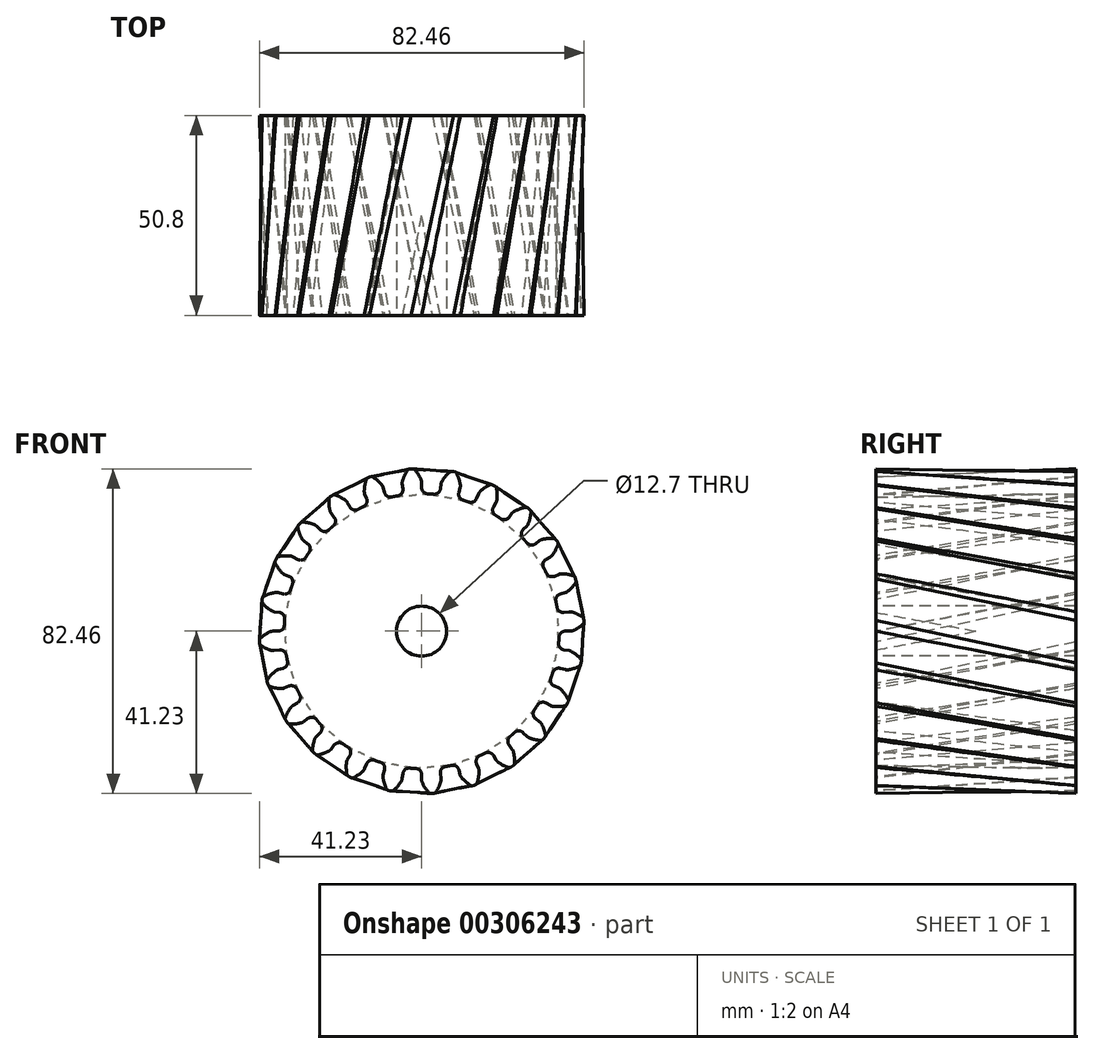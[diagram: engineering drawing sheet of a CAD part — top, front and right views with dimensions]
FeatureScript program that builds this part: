
annotation { "Feature Type Name" : "Feature", "Feature Type Description" : "" }
export const myFeature = defineFeature(function(context is Context, id is Id, definition is map)
    precondition{}
    {
        {
            var Q0;
            Q0=qCreatedBy(makeId("Front.planeOp"),FACE);
            cPlane(context, id + "F0", {"entities" : qUnion([Q0]), "cplaneType" : CPlaneType.OFFSET, "offset" : 50.8 * mm, "width" : 152.4 * mm, "height" : 152.4 * mm});
        }
        {
            var Q0;
            Q0=qCreatedBy(makeId("Front.planeOp"),FACE);
            var sketch = newSketch(context, id + "F1", { "sketchPlane" : qUnion([Q0])});
            skArc(sketch, "E0", {"start": v(-6.06, 34.4) * mm, "mid": v(-6.81, 34.25) * mm, "end": v(-7.56, 34.1) * mm});
            skArc(sketch, "E1.trimOffspring", {"start": v(-0.13, 38.41) * mm, "mid": v(-0.86, 39.8) * mm, "end": v(-1.82, 41.06) * mm});
            skLineSegment(sketch, "E2", {"start": v(0, 37.8) * mm, "end": v(0, 36.48) * mm});
            skLineSegment(sketch, "E3", {"start": v(-2.2, 41.23) * mm, "end": v(-2.7, 41.23) * mm});
            skLineSegment(sketch, "E4.MirrorCS", {"start": v(-3.2, 41.16) * mm, "end": v(-2.7, 41.23) * mm});
            skArc(sketch, "E5.MirrorCS", {"start": v(-4.89, 38.1) * mm, "mid": v(-4.34, 39.58) * mm, "end": v(-3.56, 40.95) * mm});
            skLineSegment(sketch, "E6.MirrorCS", {"start": v(-4.93, 37.47) * mm, "end": v(-4.76, 36.17) * mm});
            skPoint(sketch, "E7.visualSharp", {"position": v(0, 34.93) * mm});
            skArc(sketch, "E7.filletArc", {"start": v(0, 35.2) * mm, "mid": v(0.08, 35) * mm, "end": v(0.28, 34.92) * mm});
            skArc(sketch, "E8.filletArc", {"start": v(0, 36.48) * mm, "mid": v(0.44, 35.38) * mm, "end": v(1.52, 34.9) * mm});
            skPoint(sketch, "E9.visualSharp", {"position": v(-4.56, 34.63) * mm});
            skArc(sketch, "E9.filletArc", {"start": v(-6.06, 34.4) * mm, "mid": v(-5.06, 35.02) * mm, "end": v(-4.76, 36.17) * mm});
            skPoint(sketch, "E10.visualSharp", {"position": v(-4.97, 37.77) * mm});
            skArc(sketch, "E10.filletArc", {"start": v(-4.89, 38.1) * mm, "mid": v(-4.94, 37.79) * mm, "end": v(-4.93, 37.47) * mm});
            skPoint(sketch, "E11.visualSharp", {"position": v(0, 38.1) * mm});
            skArc(sketch, "E11.filletArc", {"start": v(0, 37.8) * mm, "mid": v(-0.03, 38.1) * mm, "end": v(-0.13, 38.41) * mm});
            skPoint(sketch, "E12.visualSharp", {"position": v(-3.43, 41.13) * mm});
            skArc(sketch, "E12.filletArc", {"start": v(-3.2, 41.16) * mm, "mid": v(-3.4, 41.1) * mm, "end": v(-3.56, 40.95) * mm});
            skPoint(sketch, "E13.visualSharp", {"position": v(-1.97, 41.23) * mm});
            skArc(sketch, "E13.filletArc", {"start": v(-1.82, 41.06) * mm, "mid": v(-1.99, 41.18) * mm, "end": v(-2.2, 41.23) * mm});
            skArc(sketch, "E14.1.0", {"start": v(-9.44, 35.24) * mm, "mid": v(-8.73, 34.29) * mm, "end": v(-7.56, 34.1) * mm});
            skLineSegment(sketch, "E14.1.1", {"start": v(-9.78, 36.5) * mm, "end": v(-9.44, 35.24) * mm});
            skLineSegment(sketch, "E14.1.2", {"start": v(-14.46, 34.91) * mm, "end": v(-13.96, 33.7) * mm});
            skLineSegment(sketch, "E14.1.3", {"start": v(-12.79, 39.26) * mm, "end": v(-13.28, 39.12) * mm});
            skPoint(sketch, "E14.1.4", {"position": v(-12.58, 39.31) * mm});
            skPoint(sketch, "E14.1.5", {"position": v(-13.96, 38.84) * mm});
            skLineSegment(sketch, "E14.1.6", {"start": v(-13.75, 38.93) * mm, "end": v(-13.28, 39.12) * mm});
            skArc(sketch, "E14.1.7", {"start": v(-10.06, 37.07) * mm, "mid": v(-11.14, 38.23) * mm, "end": v(-12.38, 39.2) * mm});
            skPoint(sketch, "E14.1.8", {"position": v(-9.86, 36.8) * mm});
            skArc(sketch, "E14.1.9", {"start": v(-14.58, 35.54) * mm, "mid": v(-14.44, 37.1) * mm, "end": v(-14.03, 38.63) * mm});
            skPoint(sketch, "E14.1.10", {"position": v(-14.58, 35.2) * mm});
            skArc(sketch, "E14.1.11", {"start": v(-14.58, 35.54) * mm, "mid": v(-14.55, 35.22) * mm, "end": v(-14.46, 34.91) * mm});
            skArc(sketch, "E14.1.12", {"start": v(-9.78, 36.5) * mm, "mid": v(-9.9, 36.8) * mm, "end": v(-10.06, 37.07) * mm});
            skArc(sketch, "E14.1.13", {"start": v(-12.38, 39.2) * mm, "mid": v(-12.58, 39.27) * mm, "end": v(-12.79, 39.26) * mm});
            skArc(sketch, "E14.1.14", {"start": v(-13.75, 38.93) * mm, "mid": v(-13.92, 38.8) * mm, "end": v(-14.03, 38.63) * mm});
            skArc(sketch, "E14.1.15", {"start": v(-14.76, 31.65) * mm, "mid": v(-13.95, 32.52) * mm, "end": v(-13.96, 33.7) * mm});
            skArc(sketch, "E14.2.0", {"start": v(-18.24, 31.6) * mm, "mid": v(-17.3, 30.86) * mm, "end": v(-16.13, 30.98) * mm});
            skLineSegment(sketch, "E14.2.1", {"start": v(-18.9, 32.73) * mm, "end": v(-18.24, 31.6) * mm});
            skLineSegment(sketch, "E14.2.2", {"start": v(-23, 29.98) * mm, "end": v(-22.2, 28.94) * mm});
            skLineSegment(sketch, "E14.2.3", {"start": v(-22.51, 34.6) * mm, "end": v(-22.95, 34.35) * mm});
            skPoint(sketch, "E14.2.4", {"position": v(-22.32, 34.72) * mm});
            skPoint(sketch, "E14.2.5", {"position": v(-23.53, 33.9) * mm});
            skLineSegment(sketch, "E14.2.6", {"start": v(-23.36, 34.04) * mm, "end": v(-22.95, 34.35) * mm});
            skArc(sketch, "E14.2.7", {"start": v(-19.32, 33.2) * mm, "mid": v(-20.65, 34.04) * mm, "end": v(-22.1, 34.65) * mm});
            skPoint(sketch, "E14.2.8", {"position": v(-19.05, 33) * mm});
            skArc(sketch, "E14.2.9", {"start": v(-23.28, 30.55) * mm, "mid": v(-23.55, 32.1) * mm, "end": v(-23.55, 33.68) * mm});
            skPoint(sketch, "E14.2.10", {"position": v(-23.2, 30.23) * mm});
            skArc(sketch, "E14.2.11", {"start": v(-23.28, 30.55) * mm, "mid": v(-23.17, 30.25) * mm, "end": v(-23, 29.98) * mm});
            skArc(sketch, "E14.2.12", {"start": v(-18.9, 32.73) * mm, "mid": v(-19.08, 32.99) * mm, "end": v(-19.32, 33.2) * mm});
            skArc(sketch, "E14.2.13", {"start": v(-22.1, 34.65) * mm, "mid": v(-22.31, 34.67) * mm, "end": v(-22.51, 34.6) * mm});
            skArc(sketch, "E14.2.14", {"start": v(-23.36, 34.04) * mm, "mid": v(-23.5, 33.88) * mm, "end": v(-23.55, 33.68) * mm});
            skArc(sketch, "E14.2.15", {"start": v(-22.45, 26.76) * mm, "mid": v(-21.89, 27.8) * mm, "end": v(-22.2, 28.94) * mm});
            skArc(sketch, "E15.3.3.0", {"start": v(-25.8, 25.8) * mm, "mid": v(-24.7, 25.33) * mm, "end": v(-23.6, 25.75) * mm});
            skLineSegment(sketch, "E15.4.3.0", {"start": v(-26.72, 26.72) * mm, "end": v(-25.8, 25.8) * mm});
            skLineSegment(sketch, "E15.7.3.0", {"start": v(-29.98, 23) * mm, "end": v(-28.94, 22.2) * mm});
            skLineSegment(sketch, "E15.10.3.0", {"start": v(-30.7, 27.6) * mm, "end": v(-31.06, 27.24) * mm});
            skPoint(sketch, "E15.13.3.0", {"position": v(-30.55, 27.76) * mm});
            skPoint(sketch, "E15.14.3.0", {"position": v(-31.5, 26.66) * mm});
            skLineSegment(sketch, "E15.15.3.0", {"start": v(-31.37, 26.84) * mm, "end": v(-31.06, 27.24) * mm});
            skArc(sketch, "E15.18.3.0", {"start": v(-27.25, 27.07) * mm, "mid": v(-28.76, 27.54) * mm, "end": v(-30.32, 27.75) * mm});
            skPoint(sketch, "E15.22.3.0", {"position": v(-26.94, 26.94) * mm});
            skArc(sketch, "E15.23.3.0", {"start": v(-30.4, 23.49) * mm, "mid": v(-31.06, 24.92) * mm, "end": v(-31.47, 26.44) * mm});
            skPoint(sketch, "E15.27.3.0", {"position": v(-30.23, 23.2) * mm});
            skArc(sketch, "E15.28.3.0", {"start": v(-30.4, 23.49) * mm, "mid": v(-30.21, 23.22) * mm, "end": v(-29.98, 23) * mm});
            skArc(sketch, "E15.32.3.0", {"start": v(-26.72, 26.72) * mm, "mid": v(-26.97, 26.92) * mm, "end": v(-27.25, 27.07) * mm});
            skArc(sketch, "E15.36.3.0", {"start": v(-30.32, 27.75) * mm, "mid": v(-30.53, 27.72) * mm, "end": v(-30.7, 27.6) * mm});
            skArc(sketch, "E15.40.3.0", {"start": v(-31.37, 26.84) * mm, "mid": v(-31.46, 26.65) * mm, "end": v(-31.47, 26.44) * mm});
            skArc(sketch, "E15.44.3.0", {"start": v(-28.6, 20.04) * mm, "mid": v(-28.34, 21.19) * mm, "end": v(-28.94, 22.2) * mm});
            skArc(sketch, "E15.3.4.0", {"start": v(-31.6, 18.24) * mm, "mid": v(-30.42, 18.07) * mm, "end": v(-29.46, 18.76) * mm});
            skLineSegment(sketch, "E15.4.4.0", {"start": v(-32.73, 18.9) * mm, "end": v(-31.6, 18.24) * mm});
            skLineSegment(sketch, "E15.7.4.0", {"start": v(-34.91, 14.46) * mm, "end": v(-33.7, 13.96) * mm});
            skLineSegment(sketch, "E15.10.4.0", {"start": v(-36.8, 18.71) * mm, "end": v(-37.06, 18.27) * mm});
            skPoint(sketch, "E15.13.4.0", {"position": v(-36.7, 18.9) * mm});
            skPoint(sketch, "E15.14.4.0", {"position": v(-37.33, 17.6) * mm});
            skLineSegment(sketch, "E15.15.4.0", {"start": v(-37.25, 17.8) * mm, "end": v(-37.06, 18.27) * mm});
            skArc(sketch, "E15.18.4.0", {"start": v(-33.33, 19.1) * mm, "mid": v(-34.9, 19.16) * mm, "end": v(-36.47, 18.96) * mm});
            skPoint(sketch, "E15.22.4.0", {"position": v(-33, 19.05) * mm});
            skArc(sketch, "E15.23.4.0", {"start": v(-35.44, 14.82) * mm, "mid": v(-36.45, 16.03) * mm, "end": v(-37.24, 17.4) * mm});
            skPoint(sketch, "E15.27.4.0", {"position": v(-35.2, 14.58) * mm});
            skArc(sketch, "E15.28.4.0", {"start": v(-35.44, 14.82) * mm, "mid": v(-35.2, 14.61) * mm, "end": v(-34.91, 14.46) * mm});
            skArc(sketch, "E15.32.4.0", {"start": v(-32.73, 18.9) * mm, "mid": v(-33.02, 19.03) * mm, "end": v(-33.33, 19.1) * mm});
            skArc(sketch, "E15.36.4.0", {"start": v(-36.47, 18.96) * mm, "mid": v(-36.66, 18.87) * mm, "end": v(-36.8, 18.71) * mm});
            skArc(sketch, "E15.40.4.0", {"start": v(-37.25, 17.8) * mm, "mid": v(-37.29, 17.6) * mm, "end": v(-37.24, 17.4) * mm});
            skArc(sketch, "E15.44.4.0", {"start": v(-32.82, 11.95) * mm, "mid": v(-32.86, 13.13) * mm, "end": v(-33.7, 13.96) * mm});
            skArc(sketch, "E15.3.5.0", {"start": v(-35.24, 9.44) * mm, "mid": v(-34.06, 9.58) * mm, "end": v(-33.31, 10.5) * mm});
            skLineSegment(sketch, "E15.4.5.0", {"start": v(-36.5, 9.78) * mm, "end": v(-35.24, 9.44) * mm});
            skLineSegment(sketch, "E15.7.5.0", {"start": v(-37.47, 4.93) * mm, "end": v(-36.17, 4.76) * mm});
            skLineSegment(sketch, "E15.10.5.0", {"start": v(-40.4, 8.55) * mm, "end": v(-40.52, 8.06) * mm});
            skPoint(sketch, "E15.13.5.0", {"position": v(-40.33, 8.77) * mm});
            skPoint(sketch, "E15.14.5.0", {"position": v(-40.62, 7.34) * mm});
            skLineSegment(sketch, "E15.15.5.0", {"start": v(-40.59, 7.56) * mm, "end": v(-40.52, 8.06) * mm});
            skArc(sketch, "E15.18.5.0", {"start": v(-37.14, 9.82) * mm, "mid": v(-38.67, 9.47) * mm, "end": v(-40.13, 8.87) * mm});
            skPoint(sketch, "E15.22.5.0", {"position": v(-36.8, 9.86) * mm});
            skArc(sketch, "E15.23.5.0", {"start": v(-38.07, 5.14) * mm, "mid": v(-39.35, 6.05) * mm, "end": v(-40.47, 7.16) * mm});
            skPoint(sketch, "E15.27.5.0", {"position": v(-37.77, 4.97) * mm});
            skArc(sketch, "E15.28.5.0", {"start": v(-38.07, 5.14) * mm, "mid": v(-37.78, 5) * mm, "end": v(-37.47, 4.93) * mm});
            skArc(sketch, "E15.32.5.0", {"start": v(-36.5, 9.78) * mm, "mid": v(-36.82, 9.83) * mm, "end": v(-37.14, 9.82) * mm});
            skArc(sketch, "E15.36.5.0", {"start": v(-40.13, 8.87) * mm, "mid": v(-40.3, 8.74) * mm, "end": v(-40.4, 8.55) * mm});
            skArc(sketch, "E15.40.5.0", {"start": v(-40.59, 7.56) * mm, "mid": v(-40.57, 7.35) * mm, "end": v(-40.47, 7.16) * mm});
            skArc(sketch, "E15.44.5.0", {"start": v(-34.8, 3.05) * mm, "mid": v(-35.13, 4.18) * mm, "end": v(-36.17, 4.76) * mm});
            skArc(sketch, "E15.3.6.0", {"start": v(-36.48, 0) * mm, "mid": v(-35.38, 0.44) * mm, "end": v(-34.9, 1.52) * mm});
            skLineSegment(sketch, "E15.4.6.0", {"start": v(-37.8, 0) * mm, "end": v(-36.48, 0) * mm});
            skLineSegment(sketch, "E15.7.6.0", {"start": v(-37.47, -4.93) * mm, "end": v(-36.17, -4.76) * mm});
            skLineSegment(sketch, "E15.10.6.0", {"start": v(-41.23, -2.2) * mm, "end": v(-41.23, -2.7) * mm});
            skPoint(sketch, "E15.13.6.0", {"position": v(-41.23, -1.97) * mm});
            skPoint(sketch, "E15.14.6.0", {"position": v(-41.13, -3.43) * mm});
            skLineSegment(sketch, "E15.15.6.0", {"start": v(-41.16, -3.2) * mm, "end": v(-41.23, -2.7) * mm});
            skArc(sketch, "E15.18.6.0", {"start": v(-38.41, -0.13) * mm, "mid": v(-39.8, -0.86) * mm, "end": v(-41.06, -1.82) * mm});
            skPoint(sketch, "E15.22.6.0", {"position": v(-38.1, 0) * mm});
            skArc(sketch, "E15.23.6.0", {"start": v(-38.1, -4.89) * mm, "mid": v(-39.58, -4.34) * mm, "end": v(-40.95, -3.56) * mm});
            skPoint(sketch, "E15.27.6.0", {"position": v(-37.77, -4.97) * mm});
            skArc(sketch, "E15.28.6.0", {"start": v(-38.1, -4.89) * mm, "mid": v(-37.79, -4.94) * mm, "end": v(-37.47, -4.93) * mm});
            skArc(sketch, "E15.32.6.0", {"start": v(-37.8, 0) * mm, "mid": v(-38.1, -0.03) * mm, "end": v(-38.41, -0.13) * mm});
            skArc(sketch, "E15.36.6.0", {"start": v(-41.06, -1.82) * mm, "mid": v(-41.18, -1.99) * mm, "end": v(-41.23, -2.2) * mm});
            skArc(sketch, "E15.40.6.0", {"start": v(-41.16, -3.2) * mm, "mid": v(-41.1, -3.4) * mm, "end": v(-40.95, -3.56) * mm});
            skArc(sketch, "E15.44.6.0", {"start": v(-34.4, -6.06) * mm, "mid": v(-35.02, -5.06) * mm, "end": v(-36.17, -4.76) * mm});
            skArc(sketch, "E15.3.7.0", {"start": v(-35.24, -9.44) * mm, "mid": v(-34.29, -8.73) * mm, "end": v(-34.1, -7.56) * mm});
            skLineSegment(sketch, "E15.4.7.0", {"start": v(-36.5, -9.78) * mm, "end": v(-35.24, -9.44) * mm});
            skLineSegment(sketch, "E15.7.7.0", {"start": v(-34.91, -14.46) * mm, "end": v(-33.7, -13.96) * mm});
            skLineSegment(sketch, "E15.10.7.0", {"start": v(-39.26, -12.79) * mm, "end": v(-39.12, -13.28) * mm});
            skPoint(sketch, "E15.13.7.0", {"position": v(-39.31, -12.58) * mm});
            skPoint(sketch, "E15.14.7.0", {"position": v(-38.84, -13.96) * mm});
            skLineSegment(sketch, "E15.15.7.0", {"start": v(-38.93, -13.75) * mm, "end": v(-39.12, -13.28) * mm});
            skArc(sketch, "E15.18.7.0", {"start": v(-37.07, -10.06) * mm, "mid": v(-38.23, -11.14) * mm, "end": v(-39.2, -12.38) * mm});
            skPoint(sketch, "E15.22.7.0", {"position": v(-36.8, -9.86) * mm});
            skArc(sketch, "E15.23.7.0", {"start": v(-35.54, -14.58) * mm, "mid": v(-37.1, -14.44) * mm, "end": v(-38.63, -14.03) * mm});
            skPoint(sketch, "E15.27.7.0", {"position": v(-35.2, -14.58) * mm});
            skArc(sketch, "E15.28.7.0", {"start": v(-35.54, -14.58) * mm, "mid": v(-35.22, -14.55) * mm, "end": v(-34.91, -14.46) * mm});
            skArc(sketch, "E15.32.7.0", {"start": v(-36.5, -9.78) * mm, "mid": v(-36.8, -9.9) * mm, "end": v(-37.07, -10.06) * mm});
            skArc(sketch, "E15.36.7.0", {"start": v(-39.2, -12.38) * mm, "mid": v(-39.27, -12.58) * mm, "end": v(-39.26, -12.79) * mm});
            skArc(sketch, "E15.40.7.0", {"start": v(-38.93, -13.75) * mm, "mid": v(-38.8, -13.92) * mm, "end": v(-38.63, -14.03) * mm});
            skArc(sketch, "E15.44.7.0", {"start": v(-31.65, -14.76) * mm, "mid": v(-32.52, -13.95) * mm, "end": v(-33.7, -13.96) * mm});
            skArc(sketch, "E15.3.8.0", {"start": v(-31.6, -18.24) * mm, "mid": v(-30.86, -17.3) * mm, "end": v(-30.98, -16.13) * mm});
            skLineSegment(sketch, "E15.4.8.0", {"start": v(-32.73, -18.9) * mm, "end": v(-31.6, -18.24) * mm});
            skLineSegment(sketch, "E15.7.8.0", {"start": v(-29.98, -23) * mm, "end": v(-28.94, -22.2) * mm});
            skLineSegment(sketch, "E15.10.8.0", {"start": v(-34.6, -22.51) * mm, "end": v(-34.35, -22.95) * mm});
            skPoint(sketch, "E15.13.8.0", {"position": v(-34.72, -22.32) * mm});
            skPoint(sketch, "E15.14.8.0", {"position": v(-33.9, -23.53) * mm});
            skLineSegment(sketch, "E15.15.8.0", {"start": v(-34.04, -23.36) * mm, "end": v(-34.35, -22.95) * mm});
            skArc(sketch, "E15.18.8.0", {"start": v(-33.2, -19.32) * mm, "mid": v(-34.04, -20.65) * mm, "end": v(-34.65, -22.1) * mm});
            skPoint(sketch, "E15.22.8.0", {"position": v(-33, -19.05) * mm});
            skArc(sketch, "E15.23.8.0", {"start": v(-30.55, -23.28) * mm, "mid": v(-32.1, -23.55) * mm, "end": v(-33.68, -23.55) * mm});
            skPoint(sketch, "E15.27.8.0", {"position": v(-30.23, -23.2) * mm});
            skArc(sketch, "E15.28.8.0", {"start": v(-30.55, -23.28) * mm, "mid": v(-30.25, -23.17) * mm, "end": v(-29.98, -23) * mm});
            skArc(sketch, "E15.32.8.0", {"start": v(-32.73, -18.9) * mm, "mid": v(-32.99, -19.08) * mm, "end": v(-33.2, -19.32) * mm});
            skArc(sketch, "E15.36.8.0", {"start": v(-34.65, -22.1) * mm, "mid": v(-34.67, -22.31) * mm, "end": v(-34.6, -22.51) * mm});
            skArc(sketch, "E15.40.8.0", {"start": v(-34.04, -23.36) * mm, "mid": v(-33.88, -23.5) * mm, "end": v(-33.68, -23.55) * mm});
            skArc(sketch, "E15.44.8.0", {"start": v(-26.76, -22.45) * mm, "mid": v(-27.8, -21.89) * mm, "end": v(-28.94, -22.2) * mm});
            skArc(sketch, "E15.3.9.0", {"start": v(-25.8, -25.8) * mm, "mid": v(-25.33, -24.7) * mm, "end": v(-25.75, -23.6) * mm});
            skLineSegment(sketch, "E15.4.9.0", {"start": v(-26.72, -26.72) * mm, "end": v(-25.8, -25.8) * mm});
            skLineSegment(sketch, "E15.7.9.0", {"start": v(-23, -29.98) * mm, "end": v(-22.2, -28.94) * mm});
            skLineSegment(sketch, "E15.10.9.0", {"start": v(-27.6, -30.7) * mm, "end": v(-27.24, -31.06) * mm});
            skPoint(sketch, "E15.13.9.0", {"position": v(-27.76, -30.55) * mm});
            skPoint(sketch, "E15.14.9.0", {"position": v(-26.66, -31.5) * mm});
            skLineSegment(sketch, "E15.15.9.0", {"start": v(-26.84, -31.37) * mm, "end": v(-27.24, -31.06) * mm});
            skArc(sketch, "E15.18.9.0", {"start": v(-27.07, -27.25) * mm, "mid": v(-27.54, -28.76) * mm, "end": v(-27.75, -30.32) * mm});
            skPoint(sketch, "E15.22.9.0", {"position": v(-26.94, -26.94) * mm});
            skArc(sketch, "E15.23.9.0", {"start": v(-23.49, -30.4) * mm, "mid": v(-24.92, -31.06) * mm, "end": v(-26.44, -31.47) * mm});
            skPoint(sketch, "E15.27.9.0", {"position": v(-23.2, -30.23) * mm});
            skArc(sketch, "E15.28.9.0", {"start": v(-23.49, -30.4) * mm, "mid": v(-23.22, -30.21) * mm, "end": v(-23, -29.98) * mm});
            skArc(sketch, "E15.32.9.0", {"start": v(-26.72, -26.72) * mm, "mid": v(-26.92, -26.97) * mm, "end": v(-27.07, -27.25) * mm});
            skArc(sketch, "E15.36.9.0", {"start": v(-27.75, -30.32) * mm, "mid": v(-27.72, -30.53) * mm, "end": v(-27.6, -30.7) * mm});
            skArc(sketch, "E15.40.9.0", {"start": v(-26.84, -31.37) * mm, "mid": v(-26.65, -31.46) * mm, "end": v(-26.44, -31.47) * mm});
            skArc(sketch, "E15.44.9.0", {"start": v(-20.04, -28.6) * mm, "mid": v(-21.19, -28.34) * mm, "end": v(-22.2, -28.94) * mm});
            skArc(sketch, "E15.3.10.0", {"start": v(-18.24, -31.6) * mm, "mid": v(-18.07, -30.42) * mm, "end": v(-18.76, -29.46) * mm});
            skLineSegment(sketch, "E15.4.10.0", {"start": v(-18.9, -32.73) * mm, "end": v(-18.24, -31.6) * mm});
            skLineSegment(sketch, "E15.7.10.0", {"start": v(-14.46, -34.91) * mm, "end": v(-13.96, -33.7) * mm});
            skLineSegment(sketch, "E15.10.10.0", {"start": v(-18.71, -36.8) * mm, "end": v(-18.27, -37.06) * mm});
            skPoint(sketch, "E15.13.10.0", {"position": v(-18.9, -36.7) * mm});
            skPoint(sketch, "E15.14.10.0", {"position": v(-17.6, -37.33) * mm});
            skLineSegment(sketch, "E15.15.10.0", {"start": v(-17.8, -37.25) * mm, "end": v(-18.27, -37.06) * mm});
            skArc(sketch, "E15.18.10.0", {"start": v(-19.1, -33.33) * mm, "mid": v(-19.16, -34.9) * mm, "end": v(-18.96, -36.47) * mm});
            skPoint(sketch, "E15.22.10.0", {"position": v(-19.05, -33) * mm});
            skArc(sketch, "E15.23.10.0", {"start": v(-14.82, -35.44) * mm, "mid": v(-16.03, -36.45) * mm, "end": v(-17.4, -37.24) * mm});
            skPoint(sketch, "E15.27.10.0", {"position": v(-14.58, -35.2) * mm});
            skArc(sketch, "E15.28.10.0", {"start": v(-14.82, -35.44) * mm, "mid": v(-14.61, -35.2) * mm, "end": v(-14.46, -34.91) * mm});
            skArc(sketch, "E15.32.10.0", {"start": v(-18.9, -32.73) * mm, "mid": v(-19.03, -33.02) * mm, "end": v(-19.1, -33.33) * mm});
            skArc(sketch, "E15.36.10.0", {"start": v(-18.96, -36.47) * mm, "mid": v(-18.87, -36.66) * mm, "end": v(-18.71, -36.8) * mm});
            skArc(sketch, "E15.40.10.0", {"start": v(-17.8, -37.25) * mm, "mid": v(-17.6, -37.29) * mm, "end": v(-17.4, -37.24) * mm});
            skArc(sketch, "E15.44.10.0", {"start": v(-11.95, -32.82) * mm, "mid": v(-13.13, -32.86) * mm, "end": v(-13.96, -33.7) * mm});
            skArc(sketch, "E15.3.11.0", {"start": v(-9.44, -35.24) * mm, "mid": v(-9.58, -34.06) * mm, "end": v(-10.5, -33.31) * mm});
            skLineSegment(sketch, "E15.4.11.0", {"start": v(-9.78, -36.5) * mm, "end": v(-9.44, -35.24) * mm});
            skLineSegment(sketch, "E15.7.11.0", {"start": v(-4.93, -37.47) * mm, "end": v(-4.76, -36.17) * mm});
            skLineSegment(sketch, "E15.10.11.0", {"start": v(-8.55, -40.4) * mm, "end": v(-8.06, -40.52) * mm});
            skPoint(sketch, "E15.13.11.0", {"position": v(-8.77, -40.33) * mm});
            skPoint(sketch, "E15.14.11.0", {"position": v(-7.34, -40.62) * mm});
            skLineSegment(sketch, "E15.15.11.0", {"start": v(-7.56, -40.59) * mm, "end": v(-8.06, -40.52) * mm});
            skArc(sketch, "E15.18.11.0", {"start": v(-9.82, -37.14) * mm, "mid": v(-9.47, -38.67) * mm, "end": v(-8.87, -40.13) * mm});
            skPoint(sketch, "E15.22.11.0", {"position": v(-9.86, -36.8) * mm});
            skArc(sketch, "E15.23.11.0", {"start": v(-5.14, -38.07) * mm, "mid": v(-6.05, -39.35) * mm, "end": v(-7.16, -40.47) * mm});
            skPoint(sketch, "E15.27.11.0", {"position": v(-4.97, -37.77) * mm});
            skArc(sketch, "E15.28.11.0", {"start": v(-5.14, -38.07) * mm, "mid": v(-5, -37.78) * mm, "end": v(-4.93, -37.47) * mm});
            skArc(sketch, "E15.32.11.0", {"start": v(-9.78, -36.5) * mm, "mid": v(-9.83, -36.82) * mm, "end": v(-9.82, -37.14) * mm});
            skArc(sketch, "E15.36.11.0", {"start": v(-8.87, -40.13) * mm, "mid": v(-8.74, -40.3) * mm, "end": v(-8.55, -40.4) * mm});
            skArc(sketch, "E15.40.11.0", {"start": v(-7.56, -40.59) * mm, "mid": v(-7.35, -40.57) * mm, "end": v(-7.16, -40.47) * mm});
            skArc(sketch, "E15.44.11.0", {"start": v(-3.05, -34.8) * mm, "mid": v(-4.18, -35.13) * mm, "end": v(-4.76, -36.17) * mm});
            skArc(sketch, "E15.3.12.0", {"start": v(0, -36.48) * mm, "mid": v(-0.44, -35.38) * mm, "end": v(-1.52, -34.9) * mm});
            skLineSegment(sketch, "E15.4.12.0", {"start": v(0, -37.8) * mm, "end": v(0, -36.48) * mm});
            skLineSegment(sketch, "E15.7.12.0", {"start": v(4.93, -37.47) * mm, "end": v(4.76, -36.17) * mm});
            skLineSegment(sketch, "E15.10.12.0", {"start": v(2.2, -41.23) * mm, "end": v(2.7, -41.23) * mm});
            skPoint(sketch, "E15.13.12.0", {"position": v(1.97, -41.23) * mm});
            skPoint(sketch, "E15.14.12.0", {"position": v(3.43, -41.13) * mm});
            skLineSegment(sketch, "E15.15.12.0", {"start": v(3.2, -41.16) * mm, "end": v(2.7, -41.23) * mm});
            skArc(sketch, "E15.18.12.0", {"start": v(0.13, -38.41) * mm, "mid": v(0.86, -39.8) * mm, "end": v(1.82, -41.06) * mm});
            skPoint(sketch, "E15.22.12.0", {"position": v(0, -38.1) * mm});
            skArc(sketch, "E15.23.12.0", {"start": v(4.89, -38.1) * mm, "mid": v(4.34, -39.58) * mm, "end": v(3.56, -40.95) * mm});
            skPoint(sketch, "E15.27.12.0", {"position": v(4.97, -37.77) * mm});
            skArc(sketch, "E15.28.12.0", {"start": v(4.89, -38.1) * mm, "mid": v(4.94, -37.79) * mm, "end": v(4.93, -37.47) * mm});
            skArc(sketch, "E15.32.12.0", {"start": v(0, -37.8) * mm, "mid": v(0.03, -38.1) * mm, "end": v(0.13, -38.41) * mm});
            skArc(sketch, "E15.36.12.0", {"start": v(1.82, -41.06) * mm, "mid": v(1.99, -41.18) * mm, "end": v(2.2, -41.23) * mm});
            skArc(sketch, "E15.40.12.0", {"start": v(3.2, -41.16) * mm, "mid": v(3.4, -41.1) * mm, "end": v(3.56, -40.95) * mm});
            skArc(sketch, "E15.44.12.0", {"start": v(6.06, -34.4) * mm, "mid": v(5.06, -35.02) * mm, "end": v(4.76, -36.17) * mm});
            skArc(sketch, "E15.3.13.0", {"start": v(9.44, -35.24) * mm, "mid": v(8.73, -34.29) * mm, "end": v(7.56, -34.1) * mm});
            skLineSegment(sketch, "E15.4.13.0", {"start": v(9.78, -36.5) * mm, "end": v(9.44, -35.24) * mm});
            skLineSegment(sketch, "E15.7.13.0", {"start": v(14.46, -34.91) * mm, "end": v(13.96, -33.7) * mm});
            skLineSegment(sketch, "E15.10.13.0", {"start": v(12.79, -39.26) * mm, "end": v(13.28, -39.12) * mm});
            skPoint(sketch, "E15.13.13.0", {"position": v(12.58, -39.31) * mm});
            skPoint(sketch, "E15.14.13.0", {"position": v(13.96, -38.84) * mm});
            skLineSegment(sketch, "E15.15.13.0", {"start": v(13.75, -38.93) * mm, "end": v(13.28, -39.12) * mm});
            skArc(sketch, "E15.18.13.0", {"start": v(10.06, -37.07) * mm, "mid": v(11.14, -38.23) * mm, "end": v(12.38, -39.2) * mm});
            skPoint(sketch, "E15.22.13.0", {"position": v(9.86, -36.8) * mm});
            skArc(sketch, "E15.23.13.0", {"start": v(14.58, -35.54) * mm, "mid": v(14.44, -37.1) * mm, "end": v(14.03, -38.63) * mm});
            skPoint(sketch, "E15.27.13.0", {"position": v(14.58, -35.2) * mm});
            skArc(sketch, "E15.28.13.0", {"start": v(14.58, -35.54) * mm, "mid": v(14.55, -35.22) * mm, "end": v(14.46, -34.91) * mm});
            skArc(sketch, "E15.32.13.0", {"start": v(9.78, -36.5) * mm, "mid": v(9.9, -36.8) * mm, "end": v(10.06, -37.07) * mm});
            skArc(sketch, "E15.36.13.0", {"start": v(12.38, -39.2) * mm, "mid": v(12.58, -39.27) * mm, "end": v(12.79, -39.26) * mm});
            skArc(sketch, "E15.40.13.0", {"start": v(13.75, -38.93) * mm, "mid": v(13.92, -38.8) * mm, "end": v(14.03, -38.63) * mm});
            skArc(sketch, "E15.44.13.0", {"start": v(14.76, -31.65) * mm, "mid": v(13.95, -32.52) * mm, "end": v(13.96, -33.7) * mm});
            skArc(sketch, "E15.3.14.0", {"start": v(18.24, -31.6) * mm, "mid": v(17.3, -30.86) * mm, "end": v(16.13, -30.98) * mm});
            skLineSegment(sketch, "E15.4.14.0", {"start": v(18.9, -32.73) * mm, "end": v(18.24, -31.6) * mm});
            skLineSegment(sketch, "E15.7.14.0", {"start": v(23, -29.98) * mm, "end": v(22.2, -28.94) * mm});
            skLineSegment(sketch, "E15.10.14.0", {"start": v(22.51, -34.6) * mm, "end": v(22.95, -34.35) * mm});
            skPoint(sketch, "E15.13.14.0", {"position": v(22.32, -34.72) * mm});
            skPoint(sketch, "E15.14.14.0", {"position": v(23.53, -33.9) * mm});
            skLineSegment(sketch, "E15.15.14.0", {"start": v(23.36, -34.04) * mm, "end": v(22.95, -34.35) * mm});
            skArc(sketch, "E15.18.14.0", {"start": v(19.32, -33.2) * mm, "mid": v(20.65, -34.04) * mm, "end": v(22.1, -34.65) * mm});
            skPoint(sketch, "E15.22.14.0", {"position": v(19.05, -33) * mm});
            skArc(sketch, "E15.23.14.0", {"start": v(23.28, -30.55) * mm, "mid": v(23.55, -32.1) * mm, "end": v(23.55, -33.68) * mm});
            skPoint(sketch, "E15.27.14.0", {"position": v(23.2, -30.23) * mm});
            skArc(sketch, "E15.28.14.0", {"start": v(23.28, -30.55) * mm, "mid": v(23.17, -30.25) * mm, "end": v(23, -29.98) * mm});
            skArc(sketch, "E15.32.14.0", {"start": v(18.9, -32.73) * mm, "mid": v(19.08, -32.99) * mm, "end": v(19.32, -33.2) * mm});
            skArc(sketch, "E15.36.14.0", {"start": v(22.1, -34.65) * mm, "mid": v(22.31, -34.67) * mm, "end": v(22.51, -34.6) * mm});
            skArc(sketch, "E15.40.14.0", {"start": v(23.36, -34.04) * mm, "mid": v(23.5, -33.88) * mm, "end": v(23.55, -33.68) * mm});
            skArc(sketch, "E15.44.14.0", {"start": v(22.45, -26.76) * mm, "mid": v(21.89, -27.8) * mm, "end": v(22.2, -28.94) * mm});
            skArc(sketch, "E15.3.15.0", {"start": v(25.8, -25.8) * mm, "mid": v(24.7, -25.33) * mm, "end": v(23.6, -25.75) * mm});
            skLineSegment(sketch, "E15.4.15.0", {"start": v(26.72, -26.72) * mm, "end": v(25.8, -25.8) * mm});
            skLineSegment(sketch, "E15.7.15.0", {"start": v(29.98, -23) * mm, "end": v(28.94, -22.2) * mm});
            skLineSegment(sketch, "E15.10.15.0", {"start": v(30.7, -27.6) * mm, "end": v(31.06, -27.24) * mm});
            skPoint(sketch, "E15.13.15.0", {"position": v(30.55, -27.76) * mm});
            skPoint(sketch, "E15.14.15.0", {"position": v(31.5, -26.66) * mm});
            skLineSegment(sketch, "E15.15.15.0", {"start": v(31.37, -26.84) * mm, "end": v(31.06, -27.24) * mm});
            skArc(sketch, "E15.18.15.0", {"start": v(27.25, -27.07) * mm, "mid": v(28.76, -27.54) * mm, "end": v(30.32, -27.75) * mm});
            skPoint(sketch, "E15.22.15.0", {"position": v(26.94, -26.94) * mm});
            skArc(sketch, "E15.23.15.0", {"start": v(30.4, -23.49) * mm, "mid": v(31.06, -24.92) * mm, "end": v(31.47, -26.44) * mm});
            skPoint(sketch, "E15.27.15.0", {"position": v(30.23, -23.2) * mm});
            skArc(sketch, "E15.28.15.0", {"start": v(30.4, -23.49) * mm, "mid": v(30.21, -23.22) * mm, "end": v(29.98, -23) * mm});
            skArc(sketch, "E15.32.15.0", {"start": v(26.72, -26.72) * mm, "mid": v(26.97, -26.92) * mm, "end": v(27.25, -27.07) * mm});
            skArc(sketch, "E15.36.15.0", {"start": v(30.32, -27.75) * mm, "mid": v(30.53, -27.72) * mm, "end": v(30.7, -27.6) * mm});
            skArc(sketch, "E15.40.15.0", {"start": v(31.37, -26.84) * mm, "mid": v(31.46, -26.65) * mm, "end": v(31.47, -26.44) * mm});
            skArc(sketch, "E15.44.15.0", {"start": v(28.6, -20.04) * mm, "mid": v(28.34, -21.19) * mm, "end": v(28.94, -22.2) * mm});
            skArc(sketch, "E15.3.16.0", {"start": v(31.6, -18.24) * mm, "mid": v(30.42, -18.07) * mm, "end": v(29.46, -18.76) * mm});
            skLineSegment(sketch, "E15.4.16.0", {"start": v(32.73, -18.9) * mm, "end": v(31.6, -18.24) * mm});
            skLineSegment(sketch, "E15.7.16.0", {"start": v(34.91, -14.46) * mm, "end": v(33.7, -13.96) * mm});
            skLineSegment(sketch, "E15.10.16.0", {"start": v(36.8, -18.71) * mm, "end": v(37.06, -18.27) * mm});
            skPoint(sketch, "E15.13.16.0", {"position": v(36.7, -18.9) * mm});
            skPoint(sketch, "E15.14.16.0", {"position": v(37.33, -17.6) * mm});
            skLineSegment(sketch, "E15.15.16.0", {"start": v(37.25, -17.8) * mm, "end": v(37.06, -18.27) * mm});
            skArc(sketch, "E15.18.16.0", {"start": v(33.33, -19.1) * mm, "mid": v(34.9, -19.16) * mm, "end": v(36.47, -18.96) * mm});
            skPoint(sketch, "E15.22.16.0", {"position": v(33, -19.05) * mm});
            skArc(sketch, "E15.23.16.0", {"start": v(35.44, -14.82) * mm, "mid": v(36.45, -16.03) * mm, "end": v(37.24, -17.4) * mm});
            skPoint(sketch, "E15.27.16.0", {"position": v(35.2, -14.58) * mm});
            skArc(sketch, "E15.28.16.0", {"start": v(35.44, -14.82) * mm, "mid": v(35.2, -14.61) * mm, "end": v(34.91, -14.46) * mm});
            skArc(sketch, "E15.32.16.0", {"start": v(32.73, -18.9) * mm, "mid": v(33.02, -19.03) * mm, "end": v(33.33, -19.1) * mm});
            skArc(sketch, "E15.36.16.0", {"start": v(36.47, -18.96) * mm, "mid": v(36.66, -18.87) * mm, "end": v(36.8, -18.71) * mm});
            skArc(sketch, "E15.40.16.0", {"start": v(37.25, -17.8) * mm, "mid": v(37.29, -17.6) * mm, "end": v(37.24, -17.4) * mm});
            skArc(sketch, "E15.44.16.0", {"start": v(32.82, -11.95) * mm, "mid": v(32.86, -13.13) * mm, "end": v(33.7, -13.96) * mm});
            skArc(sketch, "E15.3.17.0", {"start": v(35.24, -9.44) * mm, "mid": v(34.06, -9.58) * mm, "end": v(33.31, -10.5) * mm});
            skLineSegment(sketch, "E15.4.17.0", {"start": v(36.5, -9.78) * mm, "end": v(35.24, -9.44) * mm});
            skLineSegment(sketch, "E15.7.17.0", {"start": v(37.47, -4.93) * mm, "end": v(36.17, -4.76) * mm});
            skLineSegment(sketch, "E15.10.17.0", {"start": v(40.4, -8.55) * mm, "end": v(40.52, -8.06) * mm});
            skPoint(sketch, "E15.13.17.0", {"position": v(40.33, -8.77) * mm});
            skPoint(sketch, "E15.14.17.0", {"position": v(40.62, -7.34) * mm});
            skLineSegment(sketch, "E15.15.17.0", {"start": v(40.59, -7.56) * mm, "end": v(40.52, -8.06) * mm});
            skArc(sketch, "E15.18.17.0", {"start": v(37.14, -9.82) * mm, "mid": v(38.67, -9.47) * mm, "end": v(40.13, -8.87) * mm});
            skPoint(sketch, "E15.22.17.0", {"position": v(36.8, -9.86) * mm});
            skArc(sketch, "E15.23.17.0", {"start": v(38.07, -5.14) * mm, "mid": v(39.35, -6.05) * mm, "end": v(40.47, -7.16) * mm});
            skPoint(sketch, "E15.27.17.0", {"position": v(37.77, -4.97) * mm});
            skArc(sketch, "E15.28.17.0", {"start": v(38.07, -5.14) * mm, "mid": v(37.78, -5) * mm, "end": v(37.47, -4.93) * mm});
            skArc(sketch, "E15.32.17.0", {"start": v(36.5, -9.78) * mm, "mid": v(36.82, -9.83) * mm, "end": v(37.14, -9.82) * mm});
            skArc(sketch, "E15.36.17.0", {"start": v(40.13, -8.87) * mm, "mid": v(40.3, -8.74) * mm, "end": v(40.4, -8.55) * mm});
            skArc(sketch, "E15.40.17.0", {"start": v(40.59, -7.56) * mm, "mid": v(40.57, -7.35) * mm, "end": v(40.47, -7.16) * mm});
            skArc(sketch, "E15.44.17.0", {"start": v(34.8, -3.05) * mm, "mid": v(35.13, -4.18) * mm, "end": v(36.17, -4.76) * mm});
            skArc(sketch, "E15.3.18.0", {"start": v(36.48, 0) * mm, "mid": v(35.38, -0.44) * mm, "end": v(34.9, -1.52) * mm});
            skLineSegment(sketch, "E15.4.18.0", {"start": v(37.8, 0) * mm, "end": v(36.48, 0) * mm});
            skLineSegment(sketch, "E15.7.18.0", {"start": v(37.47, 4.93) * mm, "end": v(36.17, 4.76) * mm});
            skLineSegment(sketch, "E15.10.18.0", {"start": v(41.23, 2.2) * mm, "end": v(41.23, 2.7) * mm});
            skPoint(sketch, "E15.13.18.0", {"position": v(41.23, 1.97) * mm});
            skPoint(sketch, "E15.14.18.0", {"position": v(41.13, 3.43) * mm});
            skLineSegment(sketch, "E15.15.18.0", {"start": v(41.16, 3.2) * mm, "end": v(41.23, 2.7) * mm});
            skArc(sketch, "E15.18.18.0", {"start": v(38.41, 0.13) * mm, "mid": v(39.8, 0.86) * mm, "end": v(41.06, 1.82) * mm});
            skPoint(sketch, "E15.22.18.0", {"position": v(38.1, 0) * mm});
            skArc(sketch, "E15.23.18.0", {"start": v(38.1, 4.89) * mm, "mid": v(39.58, 4.34) * mm, "end": v(40.95, 3.56) * mm});
            skPoint(sketch, "E15.27.18.0", {"position": v(37.77, 4.97) * mm});
            skArc(sketch, "E15.28.18.0", {"start": v(38.1, 4.89) * mm, "mid": v(37.79, 4.94) * mm, "end": v(37.47, 4.93) * mm});
            skArc(sketch, "E15.32.18.0", {"start": v(37.8, 0) * mm, "mid": v(38.1, 0.03) * mm, "end": v(38.41, 0.13) * mm});
            skArc(sketch, "E15.36.18.0", {"start": v(41.06, 1.82) * mm, "mid": v(41.18, 1.99) * mm, "end": v(41.23, 2.2) * mm});
            skArc(sketch, "E15.40.18.0", {"start": v(41.16, 3.2) * mm, "mid": v(41.1, 3.4) * mm, "end": v(40.95, 3.56) * mm});
            skArc(sketch, "E15.44.18.0", {"start": v(34.4, 6.06) * mm, "mid": v(35.02, 5.06) * mm, "end": v(36.17, 4.76) * mm});
            skArc(sketch, "E15.3.19.0", {"start": v(35.24, 9.44) * mm, "mid": v(34.29, 8.73) * mm, "end": v(34.1, 7.56) * mm});
            skLineSegment(sketch, "E15.4.19.0", {"start": v(36.5, 9.78) * mm, "end": v(35.24, 9.44) * mm});
            skLineSegment(sketch, "E15.7.19.0", {"start": v(34.91, 14.46) * mm, "end": v(33.7, 13.96) * mm});
            skLineSegment(sketch, "E15.10.19.0", {"start": v(39.26, 12.79) * mm, "end": v(39.12, 13.28) * mm});
            skPoint(sketch, "E15.13.19.0", {"position": v(39.31, 12.58) * mm});
            skPoint(sketch, "E15.14.19.0", {"position": v(38.84, 13.96) * mm});
            skLineSegment(sketch, "E15.15.19.0", {"start": v(38.93, 13.75) * mm, "end": v(39.12, 13.28) * mm});
            skArc(sketch, "E15.18.19.0", {"start": v(37.07, 10.06) * mm, "mid": v(38.23, 11.14) * mm, "end": v(39.2, 12.38) * mm});
            skPoint(sketch, "E15.22.19.0", {"position": v(36.8, 9.86) * mm});
            skArc(sketch, "E15.23.19.0", {"start": v(35.54, 14.58) * mm, "mid": v(37.1, 14.44) * mm, "end": v(38.63, 14.03) * mm});
            skPoint(sketch, "E15.27.19.0", {"position": v(35.2, 14.58) * mm});
            skArc(sketch, "E15.28.19.0", {"start": v(35.54, 14.58) * mm, "mid": v(35.22, 14.55) * mm, "end": v(34.91, 14.46) * mm});
            skArc(sketch, "E15.32.19.0", {"start": v(36.5, 9.78) * mm, "mid": v(36.8, 9.9) * mm, "end": v(37.07, 10.06) * mm});
            skArc(sketch, "E15.36.19.0", {"start": v(39.2, 12.38) * mm, "mid": v(39.27, 12.58) * mm, "end": v(39.26, 12.79) * mm});
            skArc(sketch, "E15.40.19.0", {"start": v(38.93, 13.75) * mm, "mid": v(38.8, 13.92) * mm, "end": v(38.63, 14.03) * mm});
            skArc(sketch, "E15.44.19.0", {"start": v(31.65, 14.76) * mm, "mid": v(32.52, 13.95) * mm, "end": v(33.7, 13.96) * mm});
            skArc(sketch, "E15.3.20.0", {"start": v(31.6, 18.24) * mm, "mid": v(30.86, 17.3) * mm, "end": v(30.98, 16.13) * mm});
            skLineSegment(sketch, "E15.4.20.0", {"start": v(32.73, 18.9) * mm, "end": v(31.6, 18.24) * mm});
            skLineSegment(sketch, "E15.7.20.0", {"start": v(29.98, 23) * mm, "end": v(28.94, 22.2) * mm});
            skLineSegment(sketch, "E15.10.20.0", {"start": v(34.6, 22.51) * mm, "end": v(34.35, 22.95) * mm});
            skPoint(sketch, "E15.13.20.0", {"position": v(34.72, 22.32) * mm});
            skPoint(sketch, "E15.14.20.0", {"position": v(33.9, 23.53) * mm});
            skLineSegment(sketch, "E15.15.20.0", {"start": v(34.04, 23.36) * mm, "end": v(34.35, 22.95) * mm});
            skArc(sketch, "E15.18.20.0", {"start": v(33.2, 19.32) * mm, "mid": v(34.04, 20.65) * mm, "end": v(34.65, 22.1) * mm});
            skPoint(sketch, "E15.22.20.0", {"position": v(33, 19.05) * mm});
            skArc(sketch, "E15.23.20.0", {"start": v(30.55, 23.28) * mm, "mid": v(32.1, 23.55) * mm, "end": v(33.68, 23.55) * mm});
            skPoint(sketch, "E15.27.20.0", {"position": v(30.23, 23.2) * mm});
            skArc(sketch, "E15.28.20.0", {"start": v(30.55, 23.28) * mm, "mid": v(30.25, 23.17) * mm, "end": v(29.98, 23) * mm});
            skArc(sketch, "E15.32.20.0", {"start": v(32.73, 18.9) * mm, "mid": v(32.99, 19.08) * mm, "end": v(33.2, 19.32) * mm});
            skArc(sketch, "E15.36.20.0", {"start": v(34.65, 22.1) * mm, "mid": v(34.67, 22.31) * mm, "end": v(34.6, 22.51) * mm});
            skArc(sketch, "E15.40.20.0", {"start": v(34.04, 23.36) * mm, "mid": v(33.88, 23.5) * mm, "end": v(33.68, 23.55) * mm});
            skArc(sketch, "E15.44.20.0", {"start": v(26.76, 22.45) * mm, "mid": v(27.8, 21.89) * mm, "end": v(28.94, 22.2) * mm});
            skArc(sketch, "E15.3.21.0", {"start": v(25.8, 25.8) * mm, "mid": v(25.33, 24.7) * mm, "end": v(25.75, 23.6) * mm});
            skLineSegment(sketch, "E15.4.21.0", {"start": v(26.72, 26.72) * mm, "end": v(25.8, 25.8) * mm});
            skLineSegment(sketch, "E15.7.21.0", {"start": v(23, 29.98) * mm, "end": v(22.2, 28.94) * mm});
            skLineSegment(sketch, "E15.10.21.0", {"start": v(27.6, 30.7) * mm, "end": v(27.24, 31.06) * mm});
            skPoint(sketch, "E15.13.21.0", {"position": v(27.76, 30.55) * mm});
            skPoint(sketch, "E15.14.21.0", {"position": v(26.66, 31.5) * mm});
            skLineSegment(sketch, "E15.15.21.0", {"start": v(26.84, 31.37) * mm, "end": v(27.24, 31.06) * mm});
            skArc(sketch, "E15.18.21.0", {"start": v(27.07, 27.25) * mm, "mid": v(27.54, 28.76) * mm, "end": v(27.75, 30.32) * mm});
            skPoint(sketch, "E15.22.21.0", {"position": v(26.94, 26.94) * mm});
            skArc(sketch, "E15.23.21.0", {"start": v(23.49, 30.4) * mm, "mid": v(24.92, 31.06) * mm, "end": v(26.44, 31.47) * mm});
            skPoint(sketch, "E15.27.21.0", {"position": v(23.2, 30.23) * mm});
            skArc(sketch, "E15.28.21.0", {"start": v(23.49, 30.4) * mm, "mid": v(23.22, 30.21) * mm, "end": v(23, 29.98) * mm});
            skArc(sketch, "E15.32.21.0", {"start": v(26.72, 26.72) * mm, "mid": v(26.92, 26.97) * mm, "end": v(27.07, 27.25) * mm});
            skArc(sketch, "E15.36.21.0", {"start": v(27.75, 30.32) * mm, "mid": v(27.72, 30.53) * mm, "end": v(27.6, 30.7) * mm});
            skArc(sketch, "E15.40.21.0", {"start": v(26.84, 31.37) * mm, "mid": v(26.65, 31.46) * mm, "end": v(26.44, 31.47) * mm});
            skArc(sketch, "E15.44.21.0", {"start": v(20.04, 28.6) * mm, "mid": v(21.19, 28.34) * mm, "end": v(22.2, 28.94) * mm});
            skArc(sketch, "E15.3.22.0", {"start": v(18.24, 31.6) * mm, "mid": v(18.07, 30.42) * mm, "end": v(18.76, 29.46) * mm});
            skLineSegment(sketch, "E15.4.22.0", {"start": v(18.9, 32.73) * mm, "end": v(18.24, 31.6) * mm});
            skLineSegment(sketch, "E15.7.22.0", {"start": v(14.46, 34.91) * mm, "end": v(13.96, 33.7) * mm});
            skLineSegment(sketch, "E15.10.22.0", {"start": v(18.71, 36.8) * mm, "end": v(18.27, 37.06) * mm});
            skPoint(sketch, "E15.13.22.0", {"position": v(18.9, 36.7) * mm});
            skPoint(sketch, "E15.14.22.0", {"position": v(17.6, 37.33) * mm});
            skLineSegment(sketch, "E15.15.22.0", {"start": v(17.8, 37.25) * mm, "end": v(18.27, 37.06) * mm});
            skArc(sketch, "E15.18.22.0", {"start": v(19.1, 33.33) * mm, "mid": v(19.16, 34.9) * mm, "end": v(18.96, 36.47) * mm});
            skPoint(sketch, "E15.22.22.0", {"position": v(19.05, 33) * mm});
            skArc(sketch, "E15.23.22.0", {"start": v(14.82, 35.44) * mm, "mid": v(16.03, 36.45) * mm, "end": v(17.4, 37.24) * mm});
            skPoint(sketch, "E15.27.22.0", {"position": v(14.58, 35.2) * mm});
            skArc(sketch, "E15.28.22.0", {"start": v(14.82, 35.44) * mm, "mid": v(14.61, 35.2) * mm, "end": v(14.46, 34.91) * mm});
            skArc(sketch, "E15.32.22.0", {"start": v(18.9, 32.73) * mm, "mid": v(19.03, 33.02) * mm, "end": v(19.1, 33.33) * mm});
            skArc(sketch, "E15.36.22.0", {"start": v(18.96, 36.47) * mm, "mid": v(18.87, 36.66) * mm, "end": v(18.71, 36.8) * mm});
            skArc(sketch, "E15.40.22.0", {"start": v(17.8, 37.25) * mm, "mid": v(17.6, 37.29) * mm, "end": v(17.4, 37.24) * mm});
            skArc(sketch, "E15.44.22.0", {"start": v(11.95, 32.82) * mm, "mid": v(13.13, 32.86) * mm, "end": v(13.96, 33.7) * mm});
            skArc(sketch, "E15.3.23.0", {"start": v(9.44, 35.24) * mm, "mid": v(9.58, 34.06) * mm, "end": v(10.5, 33.31) * mm});
            skLineSegment(sketch, "E15.4.23.0", {"start": v(9.78, 36.5) * mm, "end": v(9.44, 35.24) * mm});
            skLineSegment(sketch, "E15.7.23.0", {"start": v(4.93, 37.47) * mm, "end": v(4.76, 36.17) * mm});
            skLineSegment(sketch, "E15.10.23.0", {"start": v(8.55, 40.4) * mm, "end": v(8.06, 40.52) * mm});
            skPoint(sketch, "E15.13.23.0", {"position": v(8.77, 40.33) * mm});
            skPoint(sketch, "E15.14.23.0", {"position": v(7.34, 40.62) * mm});
            skLineSegment(sketch, "E15.15.23.0", {"start": v(7.56, 40.59) * mm, "end": v(8.06, 40.52) * mm});
            skArc(sketch, "E15.18.23.0", {"start": v(9.82, 37.14) * mm, "mid": v(9.47, 38.67) * mm, "end": v(8.87, 40.13) * mm});
            skPoint(sketch, "E15.22.23.0", {"position": v(9.86, 36.8) * mm});
            skArc(sketch, "E15.23.23.0", {"start": v(5.14, 38.07) * mm, "mid": v(6.05, 39.35) * mm, "end": v(7.16, 40.47) * mm});
            skPoint(sketch, "E15.27.23.0", {"position": v(4.97, 37.77) * mm});
            skArc(sketch, "E15.28.23.0", {"start": v(5.14, 38.07) * mm, "mid": v(5, 37.78) * mm, "end": v(4.93, 37.47) * mm});
            skArc(sketch, "E15.32.23.0", {"start": v(9.78, 36.5) * mm, "mid": v(9.83, 36.82) * mm, "end": v(9.82, 37.14) * mm});
            skArc(sketch, "E15.36.23.0", {"start": v(8.87, 40.13) * mm, "mid": v(8.74, 40.3) * mm, "end": v(8.55, 40.4) * mm});
            skArc(sketch, "E15.40.23.0", {"start": v(7.56, 40.59) * mm, "mid": v(7.35, 40.57) * mm, "end": v(7.16, 40.47) * mm});
            skArc(sketch, "E15.44.23.0", {"start": v(3.05, 34.8) * mm, "mid": v(4.18, 35.13) * mm, "end": v(4.76, 36.17) * mm});
            skArc(sketch, "E16.trimOffspring", {"start": v(3.05, 34.8) * mm, "mid": v(2.28, 34.85) * mm, "end": v(1.52, 34.9) * mm});
            skArc(sketch, "E17.trimOffspring", {"start": v(11.95, 32.82) * mm, "mid": v(11.23, 33.07) * mm, "end": v(10.5, 33.31) * mm});
            skArc(sketch, "E18.trimOffspring", {"start": v(20.04, 28.6) * mm, "mid": v(19.4, 29.04) * mm, "end": v(18.76, 29.46) * mm});
            skArc(sketch, "E19.trimOffspring", {"start": v(26.76, 22.45) * mm, "mid": v(26.26, 23.03) * mm, "end": v(25.75, 23.6) * mm});
            skArc(sketch, "E20.trimOffspring", {"start": v(31.65, 14.76) * mm, "mid": v(31.32, 15.45) * mm, "end": v(30.98, 16.13) * mm});
            skArc(sketch, "E21.trimOffspring", {"start": v(34.4, 6.06) * mm, "mid": v(34.25, 6.81) * mm, "end": v(34.1, 7.56) * mm});
            skArc(sketch, "E22.trimOffspring", {"start": v(34.8, -3.05) * mm, "mid": v(34.85, -2.28) * mm, "end": v(34.9, -1.52) * mm});
            skArc(sketch, "E23.trimOffspring", {"start": v(32.82, -11.95) * mm, "mid": v(33.07, -11.23) * mm, "end": v(33.31, -10.5) * mm});
            skArc(sketch, "E24.trimOffspring", {"start": v(28.6, -20.04) * mm, "mid": v(29.04, -19.4) * mm, "end": v(29.46, -18.76) * mm});
            skArc(sketch, "E25.trimOffspring", {"start": v(22.45, -26.76) * mm, "mid": v(23.03, -26.26) * mm, "end": v(23.6, -25.75) * mm});
            skArc(sketch, "E26.trimOffspring", {"start": v(14.76, -31.65) * mm, "mid": v(15.45, -31.32) * mm, "end": v(16.13, -30.98) * mm});
            skArc(sketch, "E27.trimOffspring", {"start": v(6.06, -34.4) * mm, "mid": v(6.81, -34.25) * mm, "end": v(7.56, -34.1) * mm});
            skArc(sketch, "E28.trimOffspring", {"start": v(-3.05, -34.8) * mm, "mid": v(-2.28, -34.85) * mm, "end": v(-1.52, -34.9) * mm});
            skArc(sketch, "E29.trimOffspring", {"start": v(-11.95, -32.82) * mm, "mid": v(-11.23, -33.07) * mm, "end": v(-10.5, -33.31) * mm});
            skArc(sketch, "E30.trimOffspring", {"start": v(-20.04, -28.6) * mm, "mid": v(-19.4, -29.04) * mm, "end": v(-18.76, -29.46) * mm});
            skArc(sketch, "E31.trimOffspring", {"start": v(-26.76, -22.45) * mm, "mid": v(-26.26, -23.03) * mm, "end": v(-25.75, -23.6) * mm});
            skArc(sketch, "E32.trimOffspring", {"start": v(-31.65, -14.76) * mm, "mid": v(-31.32, -15.45) * mm, "end": v(-30.98, -16.13) * mm});
            skArc(sketch, "E33.trimOffspring", {"start": v(-34.4, -6.06) * mm, "mid": v(-34.25, -6.81) * mm, "end": v(-34.1, -7.56) * mm});
            skArc(sketch, "E34.trimOffspring", {"start": v(-34.8, 3.05) * mm, "mid": v(-34.85, 2.28) * mm, "end": v(-34.9, 1.52) * mm});
            skArc(sketch, "E35.trimOffspring", {"start": v(-32.82, 11.95) * mm, "mid": v(-33.07, 11.23) * mm, "end": v(-33.31, 10.5) * mm});
            skArc(sketch, "E36.trimOffspring", {"start": v(-28.6, 20.04) * mm, "mid": v(-29.04, 19.4) * mm, "end": v(-29.46, 18.76) * mm});
            skArc(sketch, "E37.trimOffspring", {"start": v(-22.45, 26.76) * mm, "mid": v(-23.03, 26.26) * mm, "end": v(-23.6, 25.75) * mm});
            skArc(sketch, "E38.trimOffspring", {"start": v(-14.76, 31.65) * mm, "mid": v(-15.45, 31.32) * mm, "end": v(-16.13, 30.98) * mm});
            skSolve(sketch);
        }
        {
            var Q0;
            Q0=qCreatedBy(id+"F0.planeOp",FACE);
            var sketch = newSketch(context, id + "F2", { "sketchPlane" : qUnion([Q0])});
            skArc(sketch, "E39", {"start": v(-31.65, -14.76) * mm, "mid": v(-31.32, -15.45) * mm, "end": v(-30.98, -16.13) * mm});
            skArc(sketch, "E40.trimOffspring", {"start": v(-37.07, -10.06) * mm, "mid": v(-38.23, -11.14) * mm, "end": v(-39.2, -12.38) * mm});
            skLineSegment(sketch, "E41", {"start": v(-39.26, -12.79) * mm, "end": v(-39.12, -13.28) * mm});
            skLineSegment(sketch, "E42", {"start": v(-36.5, -9.78) * mm, "end": v(-35.24, -9.44) * mm});
            skLineSegment(sketch, "E43.MirrorCS", {"start": v(-38.93, -13.75) * mm, "end": v(-39.12, -13.28) * mm});
            skArc(sketch, "E44.MirrorCS", {"start": v(-35.54, -14.58) * mm, "mid": v(-37.1, -14.44) * mm, "end": v(-38.63, -14.03) * mm});
            skLineSegment(sketch, "E45.MirrorCS", {"start": v(-34.91, -14.46) * mm, "end": v(-33.7, -13.96) * mm});
            skPoint(sketch, "E46.visualSharp", {"position": v(-32.27, -13.37) * mm});
            skArc(sketch, "E46.filletArc", {"start": v(-32.07, -13.83) * mm, "mid": v(-32.35, -13.56) * mm, "end": v(-32.73, -13.56) * mm});
            skArc(sketch, "E47.filletArc", {"start": v(-31.65, -14.76) * mm, "mid": v(-32.52, -13.95) * mm, "end": v(-33.7, -13.96) * mm});
            skPoint(sketch, "E48.visualSharp", {"position": v(-33.73, -9.04) * mm});
            skArc(sketch, "E48.filletArc", {"start": v(-35.24, -9.44) * mm, "mid": v(-34.29, -8.73) * mm, "end": v(-34.1, -7.56) * mm});
            skPoint(sketch, "E49.visualSharp", {"position": v(-36.8, -9.86) * mm});
            skArc(sketch, "E49.filletArc", {"start": v(-36.5, -9.78) * mm, "mid": v(-36.8, -9.9) * mm, "end": v(-37.07, -10.06) * mm});
            skPoint(sketch, "E50.visualSharp", {"position": v(-35.2, -14.58) * mm});
            skArc(sketch, "E50.filletArc", {"start": v(-35.54, -14.58) * mm, "mid": v(-35.22, -14.55) * mm, "end": v(-34.91, -14.46) * mm});
            skPoint(sketch, "E51.visualSharp", {"position": v(-38.84, -13.96) * mm});
            skArc(sketch, "E51.filletArc", {"start": v(-38.93, -13.75) * mm, "mid": v(-38.8, -13.92) * mm, "end": v(-38.63, -14.03) * mm});
            skPoint(sketch, "E52.visualSharp", {"position": v(-39.31, -12.58) * mm});
            skArc(sketch, "E52.filletArc", {"start": v(-39.2, -12.38) * mm, "mid": v(-39.27, -12.58) * mm, "end": v(-39.26, -12.79) * mm});
            skArc(sketch, "E53.1.0", {"start": v(-26.76, -22.45) * mm, "mid": v(-27.8, -21.89) * mm, "end": v(-28.94, -22.2) * mm});
            skLineSegment(sketch, "E53.1.1", {"start": v(-29.98, -23) * mm, "end": v(-28.94, -22.2) * mm});
            skPoint(sketch, "E53.1.2", {"position": v(-30.23, -23.2) * mm});
            skArc(sketch, "E53.1.3", {"start": v(-30.55, -23.28) * mm, "mid": v(-32.1, -23.55) * mm, "end": v(-33.68, -23.55) * mm});
            skPoint(sketch, "E53.1.4", {"position": v(-33.9, -23.53) * mm});
            skPoint(sketch, "E53.1.5", {"position": v(-33, -19.05) * mm});
            skLineSegment(sketch, "E53.1.6", {"start": v(-32.73, -18.9) * mm, "end": v(-31.6, -18.24) * mm});
            skArc(sketch, "E53.1.7", {"start": v(-33.2, -19.32) * mm, "mid": v(-34.04, -20.65) * mm, "end": v(-34.65, -22.1) * mm});
            skPoint(sketch, "E53.1.8", {"position": v(-34.72, -22.32) * mm});
            skArc(sketch, "E53.1.9", {"start": v(-32.73, -18.9) * mm, "mid": v(-32.99, -19.08) * mm, "end": v(-33.2, -19.32) * mm});
            skArc(sketch, "E53.1.10", {"start": v(-34.04, -23.36) * mm, "mid": v(-33.88, -23.5) * mm, "end": v(-33.68, -23.55) * mm});
            skLineSegment(sketch, "E53.1.11", {"start": v(-34.6, -22.51) * mm, "end": v(-34.35, -22.95) * mm});
            skArc(sketch, "E53.1.12", {"start": v(-34.65, -22.1) * mm, "mid": v(-34.67, -22.31) * mm, "end": v(-34.6, -22.51) * mm});
            skArc(sketch, "E53.1.13", {"start": v(-31.6, -18.24) * mm, "mid": v(-30.86, -17.3) * mm, "end": v(-30.98, -16.13) * mm});
            skLineSegment(sketch, "E53.1.14", {"start": v(-34.04, -23.36) * mm, "end": v(-34.35, -22.95) * mm});
            skArc(sketch, "E53.1.15", {"start": v(-30.55, -23.28) * mm, "mid": v(-30.25, -23.17) * mm, "end": v(-29.98, -23) * mm});
            skArc(sketch, "E53.2.0", {"start": v(-20.04, -28.6) * mm, "mid": v(-21.19, -28.34) * mm, "end": v(-22.2, -28.94) * mm});
            skLineSegment(sketch, "E53.2.1", {"start": v(-23, -29.98) * mm, "end": v(-22.2, -28.94) * mm});
            skPoint(sketch, "E53.2.2", {"position": v(-23.2, -30.23) * mm});
            skArc(sketch, "E53.2.3", {"start": v(-23.49, -30.4) * mm, "mid": v(-24.92, -31.06) * mm, "end": v(-26.44, -31.47) * mm});
            skPoint(sketch, "E53.2.4", {"position": v(-26.66, -31.5) * mm});
            skPoint(sketch, "E53.2.5", {"position": v(-26.94, -26.94) * mm});
            skLineSegment(sketch, "E53.2.6", {"start": v(-26.72, -26.72) * mm, "end": v(-25.8, -25.8) * mm});
            skArc(sketch, "E53.2.7", {"start": v(-27.07, -27.25) * mm, "mid": v(-27.54, -28.76) * mm, "end": v(-27.75, -30.32) * mm});
            skPoint(sketch, "E53.2.8", {"position": v(-27.76, -30.55) * mm});
            skArc(sketch, "E53.2.9", {"start": v(-26.72, -26.72) * mm, "mid": v(-26.92, -26.97) * mm, "end": v(-27.07, -27.25) * mm});
            skArc(sketch, "E53.2.10", {"start": v(-26.84, -31.37) * mm, "mid": v(-26.65, -31.46) * mm, "end": v(-26.44, -31.47) * mm});
            skLineSegment(sketch, "E53.2.11", {"start": v(-27.6, -30.7) * mm, "end": v(-27.24, -31.06) * mm});
            skArc(sketch, "E53.2.12", {"start": v(-27.75, -30.32) * mm, "mid": v(-27.72, -30.53) * mm, "end": v(-27.6, -30.7) * mm});
            skArc(sketch, "E53.2.13", {"start": v(-25.8, -25.8) * mm, "mid": v(-25.33, -24.7) * mm, "end": v(-25.75, -23.6) * mm});
            skLineSegment(sketch, "E53.2.14", {"start": v(-26.84, -31.37) * mm, "end": v(-27.24, -31.06) * mm});
            skArc(sketch, "E53.2.15", {"start": v(-23.49, -30.4) * mm, "mid": v(-23.22, -30.21) * mm, "end": v(-23, -29.98) * mm});
            skArc(sketch, "E54.1.3.0", {"start": v(-11.95, -32.82) * mm, "mid": v(-13.13, -32.86) * mm, "end": v(-13.96, -33.7) * mm});
            skLineSegment(sketch, "E54.4.3.0", {"start": v(-14.46, -34.91) * mm, "end": v(-13.96, -33.7) * mm});
            skPoint(sketch, "E54.7.3.0", {"position": v(-14.58, -35.2) * mm});
            skArc(sketch, "E54.8.3.0", {"start": v(-14.82, -35.44) * mm, "mid": v(-16.03, -36.45) * mm, "end": v(-17.4, -37.24) * mm});
            skPoint(sketch, "E54.12.3.0", {"position": v(-17.6, -37.33) * mm});
            skPoint(sketch, "E54.13.3.0", {"position": v(-19.05, -33) * mm});
            skLineSegment(sketch, "E54.14.3.0", {"start": v(-18.9, -32.73) * mm, "end": v(-18.24, -31.6) * mm});
            skArc(sketch, "E54.17.3.0", {"start": v(-19.1, -33.33) * mm, "mid": v(-19.16, -34.9) * mm, "end": v(-18.96, -36.47) * mm});
            skPoint(sketch, "E54.21.3.0", {"position": v(-18.9, -36.7) * mm});
            skArc(sketch, "E54.22.3.0", {"start": v(-18.9, -32.73) * mm, "mid": v(-19.03, -33.02) * mm, "end": v(-19.1, -33.33) * mm});
            skArc(sketch, "E54.26.3.0", {"start": v(-17.8, -37.25) * mm, "mid": v(-17.6, -37.29) * mm, "end": v(-17.4, -37.24) * mm});
            skLineSegment(sketch, "E54.30.3.0", {"start": v(-18.71, -36.8) * mm, "end": v(-18.27, -37.06) * mm});
            skArc(sketch, "E54.33.3.0", {"start": v(-18.96, -36.47) * mm, "mid": v(-18.87, -36.66) * mm, "end": v(-18.71, -36.8) * mm});
            skArc(sketch, "E54.37.3.0", {"start": v(-18.24, -31.6) * mm, "mid": v(-18.07, -30.42) * mm, "end": v(-18.76, -29.46) * mm});
            skLineSegment(sketch, "E54.41.3.0", {"start": v(-17.8, -37.25) * mm, "end": v(-18.27, -37.06) * mm});
            skArc(sketch, "E54.44.3.0", {"start": v(-14.82, -35.44) * mm, "mid": v(-14.61, -35.2) * mm, "end": v(-14.46, -34.91) * mm});
            skArc(sketch, "E54.1.4.0", {"start": v(-3.05, -34.8) * mm, "mid": v(-4.18, -35.13) * mm, "end": v(-4.76, -36.17) * mm});
            skLineSegment(sketch, "E54.4.4.0", {"start": v(-4.93, -37.47) * mm, "end": v(-4.76, -36.17) * mm});
            skPoint(sketch, "E54.7.4.0", {"position": v(-4.97, -37.77) * mm});
            skArc(sketch, "E54.8.4.0", {"start": v(-5.14, -38.07) * mm, "mid": v(-6.05, -39.35) * mm, "end": v(-7.16, -40.47) * mm});
            skPoint(sketch, "E54.12.4.0", {"position": v(-7.34, -40.62) * mm});
            skPoint(sketch, "E54.13.4.0", {"position": v(-9.86, -36.8) * mm});
            skLineSegment(sketch, "E54.14.4.0", {"start": v(-9.78, -36.5) * mm, "end": v(-9.44, -35.24) * mm});
            skArc(sketch, "E54.17.4.0", {"start": v(-9.82, -37.14) * mm, "mid": v(-9.47, -38.67) * mm, "end": v(-8.87, -40.13) * mm});
            skPoint(sketch, "E54.21.4.0", {"position": v(-8.77, -40.33) * mm});
            skArc(sketch, "E54.22.4.0", {"start": v(-9.78, -36.5) * mm, "mid": v(-9.83, -36.82) * mm, "end": v(-9.82, -37.14) * mm});
            skArc(sketch, "E54.26.4.0", {"start": v(-7.56, -40.59) * mm, "mid": v(-7.35, -40.57) * mm, "end": v(-7.16, -40.47) * mm});
            skLineSegment(sketch, "E54.30.4.0", {"start": v(-8.55, -40.4) * mm, "end": v(-8.06, -40.52) * mm});
            skArc(sketch, "E54.33.4.0", {"start": v(-8.87, -40.13) * mm, "mid": v(-8.74, -40.3) * mm, "end": v(-8.55, -40.4) * mm});
            skArc(sketch, "E54.37.4.0", {"start": v(-9.44, -35.24) * mm, "mid": v(-9.58, -34.06) * mm, "end": v(-10.5, -33.31) * mm});
            skLineSegment(sketch, "E54.41.4.0", {"start": v(-7.56, -40.59) * mm, "end": v(-8.06, -40.52) * mm});
            skArc(sketch, "E54.44.4.0", {"start": v(-5.14, -38.07) * mm, "mid": v(-5, -37.78) * mm, "end": v(-4.93, -37.47) * mm});
            skArc(sketch, "E54.1.5.0", {"start": v(6.06, -34.4) * mm, "mid": v(5.06, -35.02) * mm, "end": v(4.76, -36.17) * mm});
            skLineSegment(sketch, "E54.4.5.0", {"start": v(4.93, -37.47) * mm, "end": v(4.76, -36.17) * mm});
            skPoint(sketch, "E54.7.5.0", {"position": v(4.97, -37.77) * mm});
            skArc(sketch, "E54.8.5.0", {"start": v(4.89, -38.1) * mm, "mid": v(4.34, -39.58) * mm, "end": v(3.56, -40.95) * mm});
            skPoint(sketch, "E54.12.5.0", {"position": v(3.43, -41.13) * mm});
            skPoint(sketch, "E54.13.5.0", {"position": v(0, -38.1) * mm});
            skLineSegment(sketch, "E54.14.5.0", {"start": v(0, -37.8) * mm, "end": v(0, -36.48) * mm});
            skArc(sketch, "E54.17.5.0", {"start": v(0.13, -38.41) * mm, "mid": v(0.86, -39.8) * mm, "end": v(1.82, -41.06) * mm});
            skPoint(sketch, "E54.21.5.0", {"position": v(1.97, -41.23) * mm});
            skArc(sketch, "E54.22.5.0", {"start": v(0, -37.8) * mm, "mid": v(0.03, -38.1) * mm, "end": v(0.13, -38.41) * mm});
            skArc(sketch, "E54.26.5.0", {"start": v(3.2, -41.16) * mm, "mid": v(3.4, -41.1) * mm, "end": v(3.56, -40.95) * mm});
            skLineSegment(sketch, "E54.30.5.0", {"start": v(2.2, -41.23) * mm, "end": v(2.7, -41.23) * mm});
            skArc(sketch, "E54.33.5.0", {"start": v(1.82, -41.06) * mm, "mid": v(1.99, -41.18) * mm, "end": v(2.2, -41.23) * mm});
            skArc(sketch, "E54.37.5.0", {"start": v(0, -36.48) * mm, "mid": v(-0.44, -35.38) * mm, "end": v(-1.52, -34.9) * mm});
            skLineSegment(sketch, "E54.41.5.0", {"start": v(3.2, -41.16) * mm, "end": v(2.7, -41.23) * mm});
            skArc(sketch, "E54.44.5.0", {"start": v(4.89, -38.1) * mm, "mid": v(4.94, -37.79) * mm, "end": v(4.93, -37.47) * mm});
            skArc(sketch, "E54.1.6.0", {"start": v(14.76, -31.65) * mm, "mid": v(13.95, -32.52) * mm, "end": v(13.96, -33.7) * mm});
            skLineSegment(sketch, "E54.4.6.0", {"start": v(14.46, -34.91) * mm, "end": v(13.96, -33.7) * mm});
            skPoint(sketch, "E54.7.6.0", {"position": v(14.58, -35.2) * mm});
            skArc(sketch, "E54.8.6.0", {"start": v(14.58, -35.54) * mm, "mid": v(14.44, -37.1) * mm, "end": v(14.03, -38.63) * mm});
            skPoint(sketch, "E54.12.6.0", {"position": v(13.96, -38.84) * mm});
            skPoint(sketch, "E54.13.6.0", {"position": v(9.86, -36.8) * mm});
            skLineSegment(sketch, "E54.14.6.0", {"start": v(9.78, -36.5) * mm, "end": v(9.44, -35.24) * mm});
            skArc(sketch, "E54.17.6.0", {"start": v(10.06, -37.07) * mm, "mid": v(11.14, -38.23) * mm, "end": v(12.38, -39.2) * mm});
            skPoint(sketch, "E54.21.6.0", {"position": v(12.58, -39.31) * mm});
            skArc(sketch, "E54.22.6.0", {"start": v(9.78, -36.5) * mm, "mid": v(9.9, -36.8) * mm, "end": v(10.06, -37.07) * mm});
            skArc(sketch, "E54.26.6.0", {"start": v(13.75, -38.93) * mm, "mid": v(13.92, -38.8) * mm, "end": v(14.03, -38.63) * mm});
            skLineSegment(sketch, "E54.30.6.0", {"start": v(12.79, -39.26) * mm, "end": v(13.28, -39.12) * mm});
            skArc(sketch, "E54.33.6.0", {"start": v(12.38, -39.2) * mm, "mid": v(12.58, -39.27) * mm, "end": v(12.79, -39.26) * mm});
            skArc(sketch, "E54.37.6.0", {"start": v(9.44, -35.24) * mm, "mid": v(8.73, -34.29) * mm, "end": v(7.56, -34.1) * mm});
            skLineSegment(sketch, "E54.41.6.0", {"start": v(13.75, -38.93) * mm, "end": v(13.28, -39.12) * mm});
            skArc(sketch, "E54.44.6.0", {"start": v(14.58, -35.54) * mm, "mid": v(14.55, -35.22) * mm, "end": v(14.46, -34.91) * mm});
            skArc(sketch, "E54.1.7.0", {"start": v(22.45, -26.76) * mm, "mid": v(21.89, -27.8) * mm, "end": v(22.2, -28.94) * mm});
            skLineSegment(sketch, "E54.4.7.0", {"start": v(23, -29.98) * mm, "end": v(22.2, -28.94) * mm});
            skPoint(sketch, "E54.7.7.0", {"position": v(23.2, -30.23) * mm});
            skArc(sketch, "E54.8.7.0", {"start": v(23.28, -30.55) * mm, "mid": v(23.55, -32.1) * mm, "end": v(23.55, -33.68) * mm});
            skPoint(sketch, "E54.12.7.0", {"position": v(23.53, -33.9) * mm});
            skPoint(sketch, "E54.13.7.0", {"position": v(19.05, -33) * mm});
            skLineSegment(sketch, "E54.14.7.0", {"start": v(18.9, -32.73) * mm, "end": v(18.24, -31.6) * mm});
            skArc(sketch, "E54.17.7.0", {"start": v(19.32, -33.2) * mm, "mid": v(20.65, -34.04) * mm, "end": v(22.1, -34.65) * mm});
            skPoint(sketch, "E54.21.7.0", {"position": v(22.32, -34.72) * mm});
            skArc(sketch, "E54.22.7.0", {"start": v(18.9, -32.73) * mm, "mid": v(19.08, -32.99) * mm, "end": v(19.32, -33.2) * mm});
            skArc(sketch, "E54.26.7.0", {"start": v(23.36, -34.04) * mm, "mid": v(23.5, -33.88) * mm, "end": v(23.55, -33.68) * mm});
            skLineSegment(sketch, "E54.30.7.0", {"start": v(22.51, -34.6) * mm, "end": v(22.95, -34.35) * mm});
            skArc(sketch, "E54.33.7.0", {"start": v(22.1, -34.65) * mm, "mid": v(22.31, -34.67) * mm, "end": v(22.51, -34.6) * mm});
            skArc(sketch, "E54.37.7.0", {"start": v(18.24, -31.6) * mm, "mid": v(17.3, -30.86) * mm, "end": v(16.13, -30.98) * mm});
            skLineSegment(sketch, "E54.41.7.0", {"start": v(23.36, -34.04) * mm, "end": v(22.95, -34.35) * mm});
            skArc(sketch, "E54.44.7.0", {"start": v(23.28, -30.55) * mm, "mid": v(23.17, -30.25) * mm, "end": v(23, -29.98) * mm});
            skArc(sketch, "E54.1.8.0", {"start": v(28.6, -20.04) * mm, "mid": v(28.34, -21.19) * mm, "end": v(28.94, -22.2) * mm});
            skLineSegment(sketch, "E54.4.8.0", {"start": v(29.98, -23) * mm, "end": v(28.94, -22.2) * mm});
            skPoint(sketch, "E54.7.8.0", {"position": v(30.23, -23.2) * mm});
            skArc(sketch, "E54.8.8.0", {"start": v(30.4, -23.49) * mm, "mid": v(31.06, -24.92) * mm, "end": v(31.47, -26.44) * mm});
            skPoint(sketch, "E54.12.8.0", {"position": v(31.5, -26.66) * mm});
            skPoint(sketch, "E54.13.8.0", {"position": v(26.94, -26.94) * mm});
            skLineSegment(sketch, "E54.14.8.0", {"start": v(26.72, -26.72) * mm, "end": v(25.8, -25.8) * mm});
            skArc(sketch, "E54.17.8.0", {"start": v(27.25, -27.07) * mm, "mid": v(28.76, -27.54) * mm, "end": v(30.32, -27.75) * mm});
            skPoint(sketch, "E54.21.8.0", {"position": v(30.55, -27.76) * mm});
            skArc(sketch, "E54.22.8.0", {"start": v(26.72, -26.72) * mm, "mid": v(26.97, -26.92) * mm, "end": v(27.25, -27.07) * mm});
            skArc(sketch, "E54.26.8.0", {"start": v(31.37, -26.84) * mm, "mid": v(31.46, -26.65) * mm, "end": v(31.47, -26.44) * mm});
            skLineSegment(sketch, "E54.30.8.0", {"start": v(30.7, -27.6) * mm, "end": v(31.06, -27.24) * mm});
            skArc(sketch, "E54.33.8.0", {"start": v(30.32, -27.75) * mm, "mid": v(30.53, -27.72) * mm, "end": v(30.7, -27.6) * mm});
            skArc(sketch, "E54.37.8.0", {"start": v(25.8, -25.8) * mm, "mid": v(24.7, -25.33) * mm, "end": v(23.6, -25.75) * mm});
            skLineSegment(sketch, "E54.41.8.0", {"start": v(31.37, -26.84) * mm, "end": v(31.06, -27.24) * mm});
            skArc(sketch, "E54.44.8.0", {"start": v(30.4, -23.49) * mm, "mid": v(30.21, -23.22) * mm, "end": v(29.98, -23) * mm});
            skArc(sketch, "E54.1.9.0", {"start": v(32.82, -11.95) * mm, "mid": v(32.86, -13.13) * mm, "end": v(33.7, -13.96) * mm});
            skLineSegment(sketch, "E54.4.9.0", {"start": v(34.91, -14.46) * mm, "end": v(33.7, -13.96) * mm});
            skPoint(sketch, "E54.7.9.0", {"position": v(35.2, -14.58) * mm});
            skArc(sketch, "E54.8.9.0", {"start": v(35.44, -14.82) * mm, "mid": v(36.45, -16.03) * mm, "end": v(37.24, -17.4) * mm});
            skPoint(sketch, "E54.12.9.0", {"position": v(37.33, -17.6) * mm});
            skPoint(sketch, "E54.13.9.0", {"position": v(33, -19.05) * mm});
            skLineSegment(sketch, "E54.14.9.0", {"start": v(32.73, -18.9) * mm, "end": v(31.6, -18.24) * mm});
            skArc(sketch, "E54.17.9.0", {"start": v(33.33, -19.1) * mm, "mid": v(34.9, -19.16) * mm, "end": v(36.47, -18.96) * mm});
            skPoint(sketch, "E54.21.9.0", {"position": v(36.7, -18.9) * mm});
            skArc(sketch, "E54.22.9.0", {"start": v(32.73, -18.9) * mm, "mid": v(33.02, -19.03) * mm, "end": v(33.33, -19.1) * mm});
            skArc(sketch, "E54.26.9.0", {"start": v(37.25, -17.8) * mm, "mid": v(37.29, -17.6) * mm, "end": v(37.24, -17.4) * mm});
            skLineSegment(sketch, "E54.30.9.0", {"start": v(36.8, -18.71) * mm, "end": v(37.06, -18.27) * mm});
            skArc(sketch, "E54.33.9.0", {"start": v(36.47, -18.96) * mm, "mid": v(36.66, -18.87) * mm, "end": v(36.8, -18.71) * mm});
            skArc(sketch, "E54.37.9.0", {"start": v(31.6, -18.24) * mm, "mid": v(30.42, -18.07) * mm, "end": v(29.46, -18.76) * mm});
            skLineSegment(sketch, "E54.41.9.0", {"start": v(37.25, -17.8) * mm, "end": v(37.06, -18.27) * mm});
            skArc(sketch, "E54.44.9.0", {"start": v(35.44, -14.82) * mm, "mid": v(35.2, -14.61) * mm, "end": v(34.91, -14.46) * mm});
            skArc(sketch, "E54.1.10.0", {"start": v(34.8, -3.05) * mm, "mid": v(35.13, -4.18) * mm, "end": v(36.17, -4.76) * mm});
            skLineSegment(sketch, "E54.4.10.0", {"start": v(37.47, -4.93) * mm, "end": v(36.17, -4.76) * mm});
            skPoint(sketch, "E54.7.10.0", {"position": v(37.77, -4.97) * mm});
            skArc(sketch, "E54.8.10.0", {"start": v(38.07, -5.14) * mm, "mid": v(39.35, -6.05) * mm, "end": v(40.47, -7.16) * mm});
            skPoint(sketch, "E54.12.10.0", {"position": v(40.62, -7.34) * mm});
            skPoint(sketch, "E54.13.10.0", {"position": v(36.8, -9.86) * mm});
            skLineSegment(sketch, "E54.14.10.0", {"start": v(36.5, -9.78) * mm, "end": v(35.24, -9.44) * mm});
            skArc(sketch, "E54.17.10.0", {"start": v(37.14, -9.82) * mm, "mid": v(38.67, -9.47) * mm, "end": v(40.13, -8.87) * mm});
            skPoint(sketch, "E54.21.10.0", {"position": v(40.33, -8.77) * mm});
            skArc(sketch, "E54.22.10.0", {"start": v(36.5, -9.78) * mm, "mid": v(36.82, -9.83) * mm, "end": v(37.14, -9.82) * mm});
            skArc(sketch, "E54.26.10.0", {"start": v(40.59, -7.56) * mm, "mid": v(40.57, -7.35) * mm, "end": v(40.47, -7.16) * mm});
            skLineSegment(sketch, "E54.30.10.0", {"start": v(40.4, -8.55) * mm, "end": v(40.52, -8.06) * mm});
            skArc(sketch, "E54.33.10.0", {"start": v(40.13, -8.87) * mm, "mid": v(40.3, -8.74) * mm, "end": v(40.4, -8.55) * mm});
            skArc(sketch, "E54.37.10.0", {"start": v(35.24, -9.44) * mm, "mid": v(34.06, -9.58) * mm, "end": v(33.31, -10.5) * mm});
            skLineSegment(sketch, "E54.41.10.0", {"start": v(40.59, -7.56) * mm, "end": v(40.52, -8.06) * mm});
            skArc(sketch, "E54.44.10.0", {"start": v(38.07, -5.14) * mm, "mid": v(37.78, -5) * mm, "end": v(37.47, -4.93) * mm});
            skArc(sketch, "E54.1.11.0", {"start": v(34.4, 6.06) * mm, "mid": v(35.02, 5.06) * mm, "end": v(36.17, 4.76) * mm});
            skLineSegment(sketch, "E54.4.11.0", {"start": v(37.47, 4.93) * mm, "end": v(36.17, 4.76) * mm});
            skPoint(sketch, "E54.7.11.0", {"position": v(37.77, 4.97) * mm});
            skArc(sketch, "E54.8.11.0", {"start": v(38.1, 4.89) * mm, "mid": v(39.58, 4.34) * mm, "end": v(40.95, 3.56) * mm});
            skPoint(sketch, "E54.12.11.0", {"position": v(41.13, 3.43) * mm});
            skPoint(sketch, "E54.13.11.0", {"position": v(38.1, 0) * mm});
            skLineSegment(sketch, "E54.14.11.0", {"start": v(37.8, 0) * mm, "end": v(36.48, 0) * mm});
            skArc(sketch, "E54.17.11.0", {"start": v(38.41, 0.13) * mm, "mid": v(39.8, 0.86) * mm, "end": v(41.06, 1.82) * mm});
            skPoint(sketch, "E54.21.11.0", {"position": v(41.23, 1.97) * mm});
            skArc(sketch, "E54.22.11.0", {"start": v(37.8, 0) * mm, "mid": v(38.1, 0.03) * mm, "end": v(38.41, 0.13) * mm});
            skArc(sketch, "E54.26.11.0", {"start": v(41.16, 3.2) * mm, "mid": v(41.1, 3.4) * mm, "end": v(40.95, 3.56) * mm});
            skLineSegment(sketch, "E54.30.11.0", {"start": v(41.23, 2.2) * mm, "end": v(41.23, 2.7) * mm});
            skArc(sketch, "E54.33.11.0", {"start": v(41.06, 1.82) * mm, "mid": v(41.18, 1.99) * mm, "end": v(41.23, 2.2) * mm});
            skArc(sketch, "E54.37.11.0", {"start": v(36.48, 0) * mm, "mid": v(35.38, -0.44) * mm, "end": v(34.9, -1.52) * mm});
            skLineSegment(sketch, "E54.41.11.0", {"start": v(41.16, 3.2) * mm, "end": v(41.23, 2.7) * mm});
            skArc(sketch, "E54.44.11.0", {"start": v(38.1, 4.89) * mm, "mid": v(37.79, 4.94) * mm, "end": v(37.47, 4.93) * mm});
            skArc(sketch, "E54.1.12.0", {"start": v(31.65, 14.76) * mm, "mid": v(32.52, 13.95) * mm, "end": v(33.7, 13.96) * mm});
            skLineSegment(sketch, "E54.4.12.0", {"start": v(34.91, 14.46) * mm, "end": v(33.7, 13.96) * mm});
            skPoint(sketch, "E54.7.12.0", {"position": v(35.2, 14.58) * mm});
            skArc(sketch, "E54.8.12.0", {"start": v(35.54, 14.58) * mm, "mid": v(37.1, 14.44) * mm, "end": v(38.63, 14.03) * mm});
            skPoint(sketch, "E54.12.12.0", {"position": v(38.84, 13.96) * mm});
            skPoint(sketch, "E54.13.12.0", {"position": v(36.8, 9.86) * mm});
            skLineSegment(sketch, "E54.14.12.0", {"start": v(36.5, 9.78) * mm, "end": v(35.24, 9.44) * mm});
            skArc(sketch, "E54.17.12.0", {"start": v(37.07, 10.06) * mm, "mid": v(38.23, 11.14) * mm, "end": v(39.2, 12.38) * mm});
            skPoint(sketch, "E54.21.12.0", {"position": v(39.31, 12.58) * mm});
            skArc(sketch, "E54.22.12.0", {"start": v(36.5, 9.78) * mm, "mid": v(36.8, 9.9) * mm, "end": v(37.07, 10.06) * mm});
            skArc(sketch, "E54.26.12.0", {"start": v(38.93, 13.75) * mm, "mid": v(38.8, 13.92) * mm, "end": v(38.63, 14.03) * mm});
            skLineSegment(sketch, "E54.30.12.0", {"start": v(39.26, 12.79) * mm, "end": v(39.12, 13.28) * mm});
            skArc(sketch, "E54.33.12.0", {"start": v(39.2, 12.38) * mm, "mid": v(39.27, 12.58) * mm, "end": v(39.26, 12.79) * mm});
            skArc(sketch, "E54.37.12.0", {"start": v(35.24, 9.44) * mm, "mid": v(34.29, 8.73) * mm, "end": v(34.1, 7.56) * mm});
            skLineSegment(sketch, "E54.41.12.0", {"start": v(38.93, 13.75) * mm, "end": v(39.12, 13.28) * mm});
            skArc(sketch, "E54.44.12.0", {"start": v(35.54, 14.58) * mm, "mid": v(35.22, 14.55) * mm, "end": v(34.91, 14.46) * mm});
            skArc(sketch, "E54.1.13.0", {"start": v(26.76, 22.45) * mm, "mid": v(27.8, 21.89) * mm, "end": v(28.94, 22.2) * mm});
            skLineSegment(sketch, "E54.4.13.0", {"start": v(29.98, 23) * mm, "end": v(28.94, 22.2) * mm});
            skPoint(sketch, "E54.7.13.0", {"position": v(30.23, 23.2) * mm});
            skArc(sketch, "E54.8.13.0", {"start": v(30.55, 23.28) * mm, "mid": v(32.1, 23.55) * mm, "end": v(33.68, 23.55) * mm});
            skPoint(sketch, "E54.12.13.0", {"position": v(33.9, 23.53) * mm});
            skPoint(sketch, "E54.13.13.0", {"position": v(33, 19.05) * mm});
            skLineSegment(sketch, "E54.14.13.0", {"start": v(32.73, 18.9) * mm, "end": v(31.6, 18.24) * mm});
            skArc(sketch, "E54.17.13.0", {"start": v(33.2, 19.32) * mm, "mid": v(34.04, 20.65) * mm, "end": v(34.65, 22.1) * mm});
            skPoint(sketch, "E54.21.13.0", {"position": v(34.72, 22.32) * mm});
            skArc(sketch, "E54.22.13.0", {"start": v(32.73, 18.9) * mm, "mid": v(32.99, 19.08) * mm, "end": v(33.2, 19.32) * mm});
            skArc(sketch, "E54.26.13.0", {"start": v(34.04, 23.36) * mm, "mid": v(33.88, 23.5) * mm, "end": v(33.68, 23.55) * mm});
            skLineSegment(sketch, "E54.30.13.0", {"start": v(34.6, 22.51) * mm, "end": v(34.35, 22.95) * mm});
            skArc(sketch, "E54.33.13.0", {"start": v(34.65, 22.1) * mm, "mid": v(34.67, 22.31) * mm, "end": v(34.6, 22.51) * mm});
            skArc(sketch, "E54.37.13.0", {"start": v(31.6, 18.24) * mm, "mid": v(30.86, 17.3) * mm, "end": v(30.98, 16.13) * mm});
            skLineSegment(sketch, "E54.41.13.0", {"start": v(34.04, 23.36) * mm, "end": v(34.35, 22.95) * mm});
            skArc(sketch, "E54.44.13.0", {"start": v(30.55, 23.28) * mm, "mid": v(30.25, 23.17) * mm, "end": v(29.98, 23) * mm});
            skArc(sketch, "E54.1.14.0", {"start": v(20.04, 28.6) * mm, "mid": v(21.19, 28.34) * mm, "end": v(22.2, 28.94) * mm});
            skLineSegment(sketch, "E54.4.14.0", {"start": v(23, 29.98) * mm, "end": v(22.2, 28.94) * mm});
            skPoint(sketch, "E54.7.14.0", {"position": v(23.2, 30.23) * mm});
            skArc(sketch, "E54.8.14.0", {"start": v(23.49, 30.4) * mm, "mid": v(24.92, 31.06) * mm, "end": v(26.44, 31.47) * mm});
            skPoint(sketch, "E54.12.14.0", {"position": v(26.66, 31.5) * mm});
            skPoint(sketch, "E54.13.14.0", {"position": v(26.94, 26.94) * mm});
            skLineSegment(sketch, "E54.14.14.0", {"start": v(26.72, 26.72) * mm, "end": v(25.8, 25.8) * mm});
            skArc(sketch, "E54.17.14.0", {"start": v(27.07, 27.25) * mm, "mid": v(27.54, 28.76) * mm, "end": v(27.75, 30.32) * mm});
            skPoint(sketch, "E54.21.14.0", {"position": v(27.76, 30.55) * mm});
            skArc(sketch, "E54.22.14.0", {"start": v(26.72, 26.72) * mm, "mid": v(26.92, 26.97) * mm, "end": v(27.07, 27.25) * mm});
            skArc(sketch, "E54.26.14.0", {"start": v(26.84, 31.37) * mm, "mid": v(26.65, 31.46) * mm, "end": v(26.44, 31.47) * mm});
            skLineSegment(sketch, "E54.30.14.0", {"start": v(27.6, 30.7) * mm, "end": v(27.24, 31.06) * mm});
            skArc(sketch, "E54.33.14.0", {"start": v(27.75, 30.32) * mm, "mid": v(27.72, 30.53) * mm, "end": v(27.6, 30.7) * mm});
            skArc(sketch, "E54.37.14.0", {"start": v(25.8, 25.8) * mm, "mid": v(25.33, 24.7) * mm, "end": v(25.75, 23.6) * mm});
            skLineSegment(sketch, "E54.41.14.0", {"start": v(26.84, 31.37) * mm, "end": v(27.24, 31.06) * mm});
            skArc(sketch, "E54.44.14.0", {"start": v(23.49, 30.4) * mm, "mid": v(23.22, 30.21) * mm, "end": v(23, 29.98) * mm});
            skArc(sketch, "E54.1.15.0", {"start": v(11.95, 32.82) * mm, "mid": v(13.13, 32.86) * mm, "end": v(13.96, 33.7) * mm});
            skLineSegment(sketch, "E54.4.15.0", {"start": v(14.46, 34.91) * mm, "end": v(13.96, 33.7) * mm});
            skPoint(sketch, "E54.7.15.0", {"position": v(14.58, 35.2) * mm});
            skArc(sketch, "E54.8.15.0", {"start": v(14.82, 35.44) * mm, "mid": v(16.03, 36.45) * mm, "end": v(17.4, 37.24) * mm});
            skPoint(sketch, "E54.12.15.0", {"position": v(17.6, 37.33) * mm});
            skPoint(sketch, "E54.13.15.0", {"position": v(19.05, 33) * mm});
            skLineSegment(sketch, "E54.14.15.0", {"start": v(18.9, 32.73) * mm, "end": v(18.24, 31.6) * mm});
            skArc(sketch, "E54.17.15.0", {"start": v(19.1, 33.33) * mm, "mid": v(19.16, 34.9) * mm, "end": v(18.96, 36.47) * mm});
            skPoint(sketch, "E54.21.15.0", {"position": v(18.9, 36.7) * mm});
            skArc(sketch, "E54.22.15.0", {"start": v(18.9, 32.73) * mm, "mid": v(19.03, 33.02) * mm, "end": v(19.1, 33.33) * mm});
            skArc(sketch, "E54.26.15.0", {"start": v(17.8, 37.25) * mm, "mid": v(17.6, 37.29) * mm, "end": v(17.4, 37.24) * mm});
            skLineSegment(sketch, "E54.30.15.0", {"start": v(18.71, 36.8) * mm, "end": v(18.27, 37.06) * mm});
            skArc(sketch, "E54.33.15.0", {"start": v(18.96, 36.47) * mm, "mid": v(18.87, 36.66) * mm, "end": v(18.71, 36.8) * mm});
            skArc(sketch, "E54.37.15.0", {"start": v(18.24, 31.6) * mm, "mid": v(18.07, 30.42) * mm, "end": v(18.76, 29.46) * mm});
            skLineSegment(sketch, "E54.41.15.0", {"start": v(17.8, 37.25) * mm, "end": v(18.27, 37.06) * mm});
            skArc(sketch, "E54.44.15.0", {"start": v(14.82, 35.44) * mm, "mid": v(14.61, 35.2) * mm, "end": v(14.46, 34.91) * mm});
            skArc(sketch, "E54.1.16.0", {"start": v(3.05, 34.8) * mm, "mid": v(4.18, 35.13) * mm, "end": v(4.76, 36.17) * mm});
            skLineSegment(sketch, "E54.4.16.0", {"start": v(4.93, 37.47) * mm, "end": v(4.76, 36.17) * mm});
            skPoint(sketch, "E54.7.16.0", {"position": v(4.97, 37.77) * mm});
            skArc(sketch, "E54.8.16.0", {"start": v(5.14, 38.07) * mm, "mid": v(6.05, 39.35) * mm, "end": v(7.16, 40.47) * mm});
            skPoint(sketch, "E54.12.16.0", {"position": v(7.34, 40.62) * mm});
            skPoint(sketch, "E54.13.16.0", {"position": v(9.86, 36.8) * mm});
            skLineSegment(sketch, "E54.14.16.0", {"start": v(9.78, 36.5) * mm, "end": v(9.44, 35.24) * mm});
            skArc(sketch, "E54.17.16.0", {"start": v(9.82, 37.14) * mm, "mid": v(9.47, 38.67) * mm, "end": v(8.87, 40.13) * mm});
            skPoint(sketch, "E54.21.16.0", {"position": v(8.77, 40.33) * mm});
            skArc(sketch, "E54.22.16.0", {"start": v(9.78, 36.5) * mm, "mid": v(9.83, 36.82) * mm, "end": v(9.82, 37.14) * mm});
            skArc(sketch, "E54.26.16.0", {"start": v(7.56, 40.59) * mm, "mid": v(7.35, 40.57) * mm, "end": v(7.16, 40.47) * mm});
            skLineSegment(sketch, "E54.30.16.0", {"start": v(8.55, 40.4) * mm, "end": v(8.06, 40.52) * mm});
            skArc(sketch, "E54.33.16.0", {"start": v(8.87, 40.13) * mm, "mid": v(8.74, 40.3) * mm, "end": v(8.55, 40.4) * mm});
            skArc(sketch, "E54.37.16.0", {"start": v(9.44, 35.24) * mm, "mid": v(9.58, 34.06) * mm, "end": v(10.5, 33.31) * mm});
            skLineSegment(sketch, "E54.41.16.0", {"start": v(7.56, 40.59) * mm, "end": v(8.06, 40.52) * mm});
            skArc(sketch, "E54.44.16.0", {"start": v(5.14, 38.07) * mm, "mid": v(5, 37.78) * mm, "end": v(4.93, 37.47) * mm});
            skArc(sketch, "E54.1.17.0", {"start": v(-6.06, 34.4) * mm, "mid": v(-5.06, 35.02) * mm, "end": v(-4.76, 36.17) * mm});
            skLineSegment(sketch, "E54.4.17.0", {"start": v(-4.93, 37.47) * mm, "end": v(-4.76, 36.17) * mm});
            skPoint(sketch, "E54.7.17.0", {"position": v(-4.97, 37.77) * mm});
            skArc(sketch, "E54.8.17.0", {"start": v(-4.89, 38.1) * mm, "mid": v(-4.34, 39.58) * mm, "end": v(-3.56, 40.95) * mm});
            skPoint(sketch, "E54.12.17.0", {"position": v(-3.43, 41.13) * mm});
            skPoint(sketch, "E54.13.17.0", {"position": v(0, 38.1) * mm});
            skLineSegment(sketch, "E54.14.17.0", {"start": v(0, 37.8) * mm, "end": v(0, 36.48) * mm});
            skArc(sketch, "E54.17.17.0", {"start": v(-0.13, 38.41) * mm, "mid": v(-0.86, 39.8) * mm, "end": v(-1.82, 41.06) * mm});
            skPoint(sketch, "E54.21.17.0", {"position": v(-1.97, 41.23) * mm});
            skArc(sketch, "E54.22.17.0", {"start": v(0, 37.8) * mm, "mid": v(-0.03, 38.1) * mm, "end": v(-0.13, 38.41) * mm});
            skArc(sketch, "E54.26.17.0", {"start": v(-3.2, 41.16) * mm, "mid": v(-3.4, 41.1) * mm, "end": v(-3.56, 40.95) * mm});
            skLineSegment(sketch, "E54.30.17.0", {"start": v(-2.2, 41.23) * mm, "end": v(-2.7, 41.23) * mm});
            skArc(sketch, "E54.33.17.0", {"start": v(-1.82, 41.06) * mm, "mid": v(-1.99, 41.18) * mm, "end": v(-2.2, 41.23) * mm});
            skArc(sketch, "E54.37.17.0", {"start": v(0, 36.48) * mm, "mid": v(0.44, 35.38) * mm, "end": v(1.52, 34.9) * mm});
            skLineSegment(sketch, "E54.41.17.0", {"start": v(-3.2, 41.16) * mm, "end": v(-2.7, 41.23) * mm});
            skArc(sketch, "E54.44.17.0", {"start": v(-4.89, 38.1) * mm, "mid": v(-4.94, 37.79) * mm, "end": v(-4.93, 37.47) * mm});
            skArc(sketch, "E54.1.18.0", {"start": v(-14.76, 31.65) * mm, "mid": v(-13.95, 32.52) * mm, "end": v(-13.96, 33.7) * mm});
            skLineSegment(sketch, "E54.4.18.0", {"start": v(-14.46, 34.91) * mm, "end": v(-13.96, 33.7) * mm});
            skPoint(sketch, "E54.7.18.0", {"position": v(-14.58, 35.2) * mm});
            skArc(sketch, "E54.8.18.0", {"start": v(-14.58, 35.54) * mm, "mid": v(-14.44, 37.1) * mm, "end": v(-14.03, 38.63) * mm});
            skPoint(sketch, "E54.12.18.0", {"position": v(-13.96, 38.84) * mm});
            skPoint(sketch, "E54.13.18.0", {"position": v(-9.86, 36.8) * mm});
            skLineSegment(sketch, "E54.14.18.0", {"start": v(-9.78, 36.5) * mm, "end": v(-9.44, 35.24) * mm});
            skArc(sketch, "E54.17.18.0", {"start": v(-10.06, 37.07) * mm, "mid": v(-11.14, 38.23) * mm, "end": v(-12.38, 39.2) * mm});
            skPoint(sketch, "E54.21.18.0", {"position": v(-12.58, 39.31) * mm});
            skArc(sketch, "E54.22.18.0", {"start": v(-9.78, 36.5) * mm, "mid": v(-9.9, 36.8) * mm, "end": v(-10.06, 37.07) * mm});
            skArc(sketch, "E54.26.18.0", {"start": v(-13.75, 38.93) * mm, "mid": v(-13.92, 38.8) * mm, "end": v(-14.03, 38.63) * mm});
            skLineSegment(sketch, "E54.30.18.0", {"start": v(-12.79, 39.26) * mm, "end": v(-13.28, 39.12) * mm});
            skArc(sketch, "E54.33.18.0", {"start": v(-12.38, 39.2) * mm, "mid": v(-12.58, 39.27) * mm, "end": v(-12.79, 39.26) * mm});
            skArc(sketch, "E54.37.18.0", {"start": v(-9.44, 35.24) * mm, "mid": v(-8.73, 34.29) * mm, "end": v(-7.56, 34.1) * mm});
            skLineSegment(sketch, "E54.41.18.0", {"start": v(-13.75, 38.93) * mm, "end": v(-13.28, 39.12) * mm});
            skArc(sketch, "E54.44.18.0", {"start": v(-14.58, 35.54) * mm, "mid": v(-14.55, 35.22) * mm, "end": v(-14.46, 34.91) * mm});
            skArc(sketch, "E54.1.19.0", {"start": v(-22.45, 26.76) * mm, "mid": v(-21.89, 27.8) * mm, "end": v(-22.2, 28.94) * mm});
            skLineSegment(sketch, "E54.4.19.0", {"start": v(-23, 29.98) * mm, "end": v(-22.2, 28.94) * mm});
            skPoint(sketch, "E54.7.19.0", {"position": v(-23.2, 30.23) * mm});
            skArc(sketch, "E54.8.19.0", {"start": v(-23.28, 30.55) * mm, "mid": v(-23.55, 32.1) * mm, "end": v(-23.55, 33.68) * mm});
            skPoint(sketch, "E54.12.19.0", {"position": v(-23.53, 33.9) * mm});
            skPoint(sketch, "E54.13.19.0", {"position": v(-19.05, 33) * mm});
            skLineSegment(sketch, "E54.14.19.0", {"start": v(-18.9, 32.73) * mm, "end": v(-18.24, 31.6) * mm});
            skArc(sketch, "E54.17.19.0", {"start": v(-19.32, 33.2) * mm, "mid": v(-20.65, 34.04) * mm, "end": v(-22.1, 34.65) * mm});
            skPoint(sketch, "E54.21.19.0", {"position": v(-22.32, 34.72) * mm});
            skArc(sketch, "E54.22.19.0", {"start": v(-18.9, 32.73) * mm, "mid": v(-19.08, 32.99) * mm, "end": v(-19.32, 33.2) * mm});
            skArc(sketch, "E54.26.19.0", {"start": v(-23.36, 34.04) * mm, "mid": v(-23.5, 33.88) * mm, "end": v(-23.55, 33.68) * mm});
            skLineSegment(sketch, "E54.30.19.0", {"start": v(-22.51, 34.6) * mm, "end": v(-22.95, 34.35) * mm});
            skArc(sketch, "E54.33.19.0", {"start": v(-22.1, 34.65) * mm, "mid": v(-22.31, 34.67) * mm, "end": v(-22.51, 34.6) * mm});
            skArc(sketch, "E54.37.19.0", {"start": v(-18.24, 31.6) * mm, "mid": v(-17.3, 30.86) * mm, "end": v(-16.13, 30.98) * mm});
            skLineSegment(sketch, "E54.41.19.0", {"start": v(-23.36, 34.04) * mm, "end": v(-22.95, 34.35) * mm});
            skArc(sketch, "E54.44.19.0", {"start": v(-23.28, 30.55) * mm, "mid": v(-23.17, 30.25) * mm, "end": v(-23, 29.98) * mm});
            skArc(sketch, "E54.1.20.0", {"start": v(-28.6, 20.04) * mm, "mid": v(-28.34, 21.19) * mm, "end": v(-28.94, 22.2) * mm});
            skLineSegment(sketch, "E54.4.20.0", {"start": v(-29.98, 23) * mm, "end": v(-28.94, 22.2) * mm});
            skPoint(sketch, "E54.7.20.0", {"position": v(-30.23, 23.2) * mm});
            skArc(sketch, "E54.8.20.0", {"start": v(-30.4, 23.49) * mm, "mid": v(-31.06, 24.92) * mm, "end": v(-31.47, 26.44) * mm});
            skPoint(sketch, "E54.12.20.0", {"position": v(-31.5, 26.66) * mm});
            skPoint(sketch, "E54.13.20.0", {"position": v(-26.94, 26.94) * mm});
            skLineSegment(sketch, "E54.14.20.0", {"start": v(-26.72, 26.72) * mm, "end": v(-25.8, 25.8) * mm});
            skArc(sketch, "E54.17.20.0", {"start": v(-27.25, 27.07) * mm, "mid": v(-28.76, 27.54) * mm, "end": v(-30.32, 27.75) * mm});
            skPoint(sketch, "E54.21.20.0", {"position": v(-30.55, 27.76) * mm});
            skArc(sketch, "E54.22.20.0", {"start": v(-26.72, 26.72) * mm, "mid": v(-26.97, 26.92) * mm, "end": v(-27.25, 27.07) * mm});
            skArc(sketch, "E54.26.20.0", {"start": v(-31.37, 26.84) * mm, "mid": v(-31.46, 26.65) * mm, "end": v(-31.47, 26.44) * mm});
            skLineSegment(sketch, "E54.30.20.0", {"start": v(-30.7, 27.6) * mm, "end": v(-31.06, 27.24) * mm});
            skArc(sketch, "E54.33.20.0", {"start": v(-30.32, 27.75) * mm, "mid": v(-30.53, 27.72) * mm, "end": v(-30.7, 27.6) * mm});
            skArc(sketch, "E54.37.20.0", {"start": v(-25.8, 25.8) * mm, "mid": v(-24.7, 25.33) * mm, "end": v(-23.6, 25.75) * mm});
            skLineSegment(sketch, "E54.41.20.0", {"start": v(-31.37, 26.84) * mm, "end": v(-31.06, 27.24) * mm});
            skArc(sketch, "E54.44.20.0", {"start": v(-30.4, 23.49) * mm, "mid": v(-30.21, 23.22) * mm, "end": v(-29.98, 23) * mm});
            skArc(sketch, "E54.1.21.0", {"start": v(-32.82, 11.95) * mm, "mid": v(-32.86, 13.13) * mm, "end": v(-33.7, 13.96) * mm});
            skLineSegment(sketch, "E54.4.21.0", {"start": v(-34.91, 14.46) * mm, "end": v(-33.7, 13.96) * mm});
            skPoint(sketch, "E54.7.21.0", {"position": v(-35.2, 14.58) * mm});
            skArc(sketch, "E54.8.21.0", {"start": v(-35.44, 14.82) * mm, "mid": v(-36.45, 16.03) * mm, "end": v(-37.24, 17.4) * mm});
            skPoint(sketch, "E54.12.21.0", {"position": v(-37.33, 17.6) * mm});
            skPoint(sketch, "E54.13.21.0", {"position": v(-33, 19.05) * mm});
            skLineSegment(sketch, "E54.14.21.0", {"start": v(-32.73, 18.9) * mm, "end": v(-31.6, 18.24) * mm});
            skArc(sketch, "E54.17.21.0", {"start": v(-33.33, 19.1) * mm, "mid": v(-34.9, 19.16) * mm, "end": v(-36.47, 18.96) * mm});
            skPoint(sketch, "E54.21.21.0", {"position": v(-36.7, 18.9) * mm});
            skArc(sketch, "E54.22.21.0", {"start": v(-32.73, 18.9) * mm, "mid": v(-33.02, 19.03) * mm, "end": v(-33.33, 19.1) * mm});
            skArc(sketch, "E54.26.21.0", {"start": v(-37.25, 17.8) * mm, "mid": v(-37.29, 17.6) * mm, "end": v(-37.24, 17.4) * mm});
            skLineSegment(sketch, "E54.30.21.0", {"start": v(-36.8, 18.71) * mm, "end": v(-37.06, 18.27) * mm});
            skArc(sketch, "E54.33.21.0", {"start": v(-36.47, 18.96) * mm, "mid": v(-36.66, 18.87) * mm, "end": v(-36.8, 18.71) * mm});
            skArc(sketch, "E54.37.21.0", {"start": v(-31.6, 18.24) * mm, "mid": v(-30.42, 18.07) * mm, "end": v(-29.46, 18.76) * mm});
            skLineSegment(sketch, "E54.41.21.0", {"start": v(-37.25, 17.8) * mm, "end": v(-37.06, 18.27) * mm});
            skArc(sketch, "E54.44.21.0", {"start": v(-35.44, 14.82) * mm, "mid": v(-35.2, 14.61) * mm, "end": v(-34.91, 14.46) * mm});
            skArc(sketch, "E54.1.22.0", {"start": v(-34.8, 3.05) * mm, "mid": v(-35.13, 4.18) * mm, "end": v(-36.17, 4.76) * mm});
            skLineSegment(sketch, "E54.4.22.0", {"start": v(-37.47, 4.93) * mm, "end": v(-36.17, 4.76) * mm});
            skPoint(sketch, "E54.7.22.0", {"position": v(-37.77, 4.97) * mm});
            skArc(sketch, "E54.8.22.0", {"start": v(-38.07, 5.14) * mm, "mid": v(-39.35, 6.05) * mm, "end": v(-40.47, 7.16) * mm});
            skPoint(sketch, "E54.12.22.0", {"position": v(-40.62, 7.34) * mm});
            skPoint(sketch, "E54.13.22.0", {"position": v(-36.8, 9.86) * mm});
            skLineSegment(sketch, "E54.14.22.0", {"start": v(-36.5, 9.78) * mm, "end": v(-35.24, 9.44) * mm});
            skArc(sketch, "E54.17.22.0", {"start": v(-37.14, 9.82) * mm, "mid": v(-38.67, 9.47) * mm, "end": v(-40.13, 8.87) * mm});
            skPoint(sketch, "E54.21.22.0", {"position": v(-40.33, 8.77) * mm});
            skArc(sketch, "E54.22.22.0", {"start": v(-36.5, 9.78) * mm, "mid": v(-36.82, 9.83) * mm, "end": v(-37.14, 9.82) * mm});
            skArc(sketch, "E54.26.22.0", {"start": v(-40.59, 7.56) * mm, "mid": v(-40.57, 7.35) * mm, "end": v(-40.47, 7.16) * mm});
            skLineSegment(sketch, "E54.30.22.0", {"start": v(-40.4, 8.55) * mm, "end": v(-40.52, 8.06) * mm});
            skArc(sketch, "E54.33.22.0", {"start": v(-40.13, 8.87) * mm, "mid": v(-40.3, 8.74) * mm, "end": v(-40.4, 8.55) * mm});
            skArc(sketch, "E54.37.22.0", {"start": v(-35.24, 9.44) * mm, "mid": v(-34.06, 9.58) * mm, "end": v(-33.31, 10.5) * mm});
            skLineSegment(sketch, "E54.41.22.0", {"start": v(-40.59, 7.56) * mm, "end": v(-40.52, 8.06) * mm});
            skArc(sketch, "E54.44.22.0", {"start": v(-38.07, 5.14) * mm, "mid": v(-37.78, 5) * mm, "end": v(-37.47, 4.93) * mm});
            skArc(sketch, "E54.1.23.0", {"start": v(-34.4, -6.06) * mm, "mid": v(-35.02, -5.06) * mm, "end": v(-36.17, -4.76) * mm});
            skLineSegment(sketch, "E54.4.23.0", {"start": v(-37.47, -4.93) * mm, "end": v(-36.17, -4.76) * mm});
            skPoint(sketch, "E54.7.23.0", {"position": v(-37.77, -4.97) * mm});
            skArc(sketch, "E54.8.23.0", {"start": v(-38.1, -4.89) * mm, "mid": v(-39.58, -4.34) * mm, "end": v(-40.95, -3.56) * mm});
            skPoint(sketch, "E54.12.23.0", {"position": v(-41.13, -3.43) * mm});
            skPoint(sketch, "E54.13.23.0", {"position": v(-38.1, 0) * mm});
            skLineSegment(sketch, "E54.14.23.0", {"start": v(-37.8, 0) * mm, "end": v(-36.48, 0) * mm});
            skArc(sketch, "E54.17.23.0", {"start": v(-38.41, -0.13) * mm, "mid": v(-39.8, -0.86) * mm, "end": v(-41.06, -1.82) * mm});
            skPoint(sketch, "E54.21.23.0", {"position": v(-41.23, -1.97) * mm});
            skArc(sketch, "E54.22.23.0", {"start": v(-37.8, 0) * mm, "mid": v(-38.1, -0.03) * mm, "end": v(-38.41, -0.13) * mm});
            skArc(sketch, "E54.26.23.0", {"start": v(-41.16, -3.2) * mm, "mid": v(-41.1, -3.4) * mm, "end": v(-40.95, -3.56) * mm});
            skLineSegment(sketch, "E54.30.23.0", {"start": v(-41.23, -2.2) * mm, "end": v(-41.23, -2.7) * mm});
            skArc(sketch, "E54.33.23.0", {"start": v(-41.06, -1.82) * mm, "mid": v(-41.18, -1.99) * mm, "end": v(-41.23, -2.2) * mm});
            skArc(sketch, "E54.37.23.0", {"start": v(-36.48, 0) * mm, "mid": v(-35.38, 0.44) * mm, "end": v(-34.9, 1.52) * mm});
            skLineSegment(sketch, "E54.41.23.0", {"start": v(-41.16, -3.2) * mm, "end": v(-41.23, -2.7) * mm});
            skArc(sketch, "E54.44.23.0", {"start": v(-38.1, -4.89) * mm, "mid": v(-37.79, -4.94) * mm, "end": v(-37.47, -4.93) * mm});
            skArc(sketch, "E55.trimOffspring", {"start": v(-34.4, -6.06) * mm, "mid": v(-34.25, -6.81) * mm, "end": v(-34.1, -7.56) * mm});
            skArc(sketch, "E56.trimOffspring", {"start": v(-34.8, 3.05) * mm, "mid": v(-34.85, 2.28) * mm, "end": v(-34.9, 1.52) * mm});
            skArc(sketch, "E57.trimOffspring", {"start": v(-32.82, 11.95) * mm, "mid": v(-33.07, 11.23) * mm, "end": v(-33.31, 10.5) * mm});
            skArc(sketch, "E58.trimOffspring", {"start": v(-28.6, 20.04) * mm, "mid": v(-29.04, 19.4) * mm, "end": v(-29.46, 18.76) * mm});
            skArc(sketch, "E59.trimOffspring", {"start": v(-22.45, 26.76) * mm, "mid": v(-23.03, 26.26) * mm, "end": v(-23.6, 25.75) * mm});
            skArc(sketch, "E60.trimOffspring", {"start": v(-14.76, 31.65) * mm, "mid": v(-15.45, 31.32) * mm, "end": v(-16.13, 30.98) * mm});
            skArc(sketch, "E61.trimOffspring", {"start": v(-6.06, 34.4) * mm, "mid": v(-6.81, 34.25) * mm, "end": v(-7.56, 34.1) * mm});
            skArc(sketch, "E62.trimOffspring", {"start": v(3.05, 34.8) * mm, "mid": v(2.28, 34.85) * mm, "end": v(1.52, 34.9) * mm});
            skArc(sketch, "E63.trimOffspring", {"start": v(11.95, 32.82) * mm, "mid": v(11.23, 33.07) * mm, "end": v(10.5, 33.31) * mm});
            skArc(sketch, "E64.trimOffspring", {"start": v(20.04, 28.6) * mm, "mid": v(19.4, 29.04) * mm, "end": v(18.76, 29.46) * mm});
            skArc(sketch, "E65.trimOffspring", {"start": v(26.76, 22.45) * mm, "mid": v(26.26, 23.03) * mm, "end": v(25.75, 23.6) * mm});
            skArc(sketch, "E66.trimOffspring", {"start": v(31.65, 14.76) * mm, "mid": v(31.32, 15.45) * mm, "end": v(30.98, 16.13) * mm});
            skArc(sketch, "E67.trimOffspring", {"start": v(34.4, 6.06) * mm, "mid": v(34.25, 6.81) * mm, "end": v(34.1, 7.56) * mm});
            skArc(sketch, "E68.trimOffspring", {"start": v(34.8, -3.05) * mm, "mid": v(34.85, -2.28) * mm, "end": v(34.9, -1.52) * mm});
            skArc(sketch, "E69.trimOffspring", {"start": v(32.82, -11.95) * mm, "mid": v(33.07, -11.23) * mm, "end": v(33.31, -10.5) * mm});
            skArc(sketch, "E70.trimOffspring", {"start": v(28.6, -20.04) * mm, "mid": v(29.04, -19.4) * mm, "end": v(29.46, -18.76) * mm});
            skArc(sketch, "E71.trimOffspring", {"start": v(14.76, -31.65) * mm, "mid": v(15.45, -31.32) * mm, "end": v(16.13, -30.98) * mm});
            skArc(sketch, "E72.trimOffspring", {"start": v(22.45, -26.76) * mm, "mid": v(23.03, -26.26) * mm, "end": v(23.6, -25.75) * mm});
            skArc(sketch, "E73.trimOffspring", {"start": v(6.06, -34.4) * mm, "mid": v(6.81, -34.25) * mm, "end": v(7.56, -34.1) * mm});
            skArc(sketch, "E74.trimOffspring", {"start": v(-3.05, -34.8) * mm, "mid": v(-2.28, -34.85) * mm, "end": v(-1.52, -34.9) * mm});
            skArc(sketch, "E75.trimOffspring", {"start": v(-11.95, -32.82) * mm, "mid": v(-11.23, -33.07) * mm, "end": v(-10.5, -33.31) * mm});
            skArc(sketch, "E76.trimOffspring", {"start": v(-20.04, -28.6) * mm, "mid": v(-19.4, -29.04) * mm, "end": v(-18.76, -29.46) * mm});
            skArc(sketch, "E77.trimOffspring", {"start": v(-26.76, -22.45) * mm, "mid": v(-26.26, -23.03) * mm, "end": v(-25.75, -23.6) * mm});
            skLineSegment(sketch, "E78", {"start": v(0, 0) * mm, "end": v(3, -11.17) * mm});
            skSolve(sketch);
        }
        {
            var Q0;
            Q0=makeQuery(id+"F1.imprint","IMPRINT",FACE,{"disambiguationData":[TD([[makeQuery(id+"F1.imprint","IMPRINT",EDGE,{"derivedFrom":sQuery(id+"F1.wireOp",EDGE,"E0")}),1.0]])]});
            var Q1;
            Q1=makeQuery(id+"F2.imprint","IMPRINT",FACE,{"disambiguationData":[TD([[makeQuery(id+"F2.imprint","IMPRINT",EDGE,{"derivedFrom":sQuery(id+"F2.wireOp",EDGE,"E39")}),1.0]])]});
            var Q2;
            Q2=sQuery(id+"F2.wireOp",VERTEX,"E54.41.18.0.end");
            var Q3;
            Q3=sQuery(id+"F1.wireOp",VERTEX,"E4.MirrorCS.end");
            loft(context, id + "F3", {"sheetProfilesArray" : [{ "sheetProfileEntities" : qUnion([Q0]) }, { "sheetProfileEntities" : qUnion([Q1]) }], "matchConnections" : true, "connections" : [{ "connectionEntities" : qUnion([Q2, Q3]), "connectionEdgeQueries" : qUnion([]), "connectionEdgeParameters" : [] }]});
        }
        {
            var Q0;
            Q0=sQuery(id+"F2.wireOp",VERTEX,"E39.center");
            var Q1;
            Q1=makeQuery(id+"F3.opLoft","SWEPT_BODY",BODY,{"disambiguationData":[OSD([makeQuery(id+"F1.imprint","IMPRINT",FACE,{"disambiguationData":[TD([[makeQuery(id+"F1.imprint","IMPRINT",EDGE,{"derivedFrom":sQuery(id+"F1.wireOp",EDGE,"E0")}),1.0]])]}),makeQuery(id+"F2.imprint","IMPRINT",FACE,{"disambiguationData":[TD([[makeQuery(id+"F2.imprint","IMPRINT",EDGE,{"derivedFrom":sQuery(id+"F2.wireOp",EDGE,"E39")}),1.0]])]})])]});
            hole(context, id + "F4", {"style" : HoleStyle.SIMPLE, "endStyle" : HoleEndStyle.THROUGH, "holeDiameter" : 12.7 * mm, "tappedDepth" : 12.7 * mm, "tapClearance" : 3, "locations" : qUnion([Q0]), "scope" : qUnion([Q1])});
        }
    });
